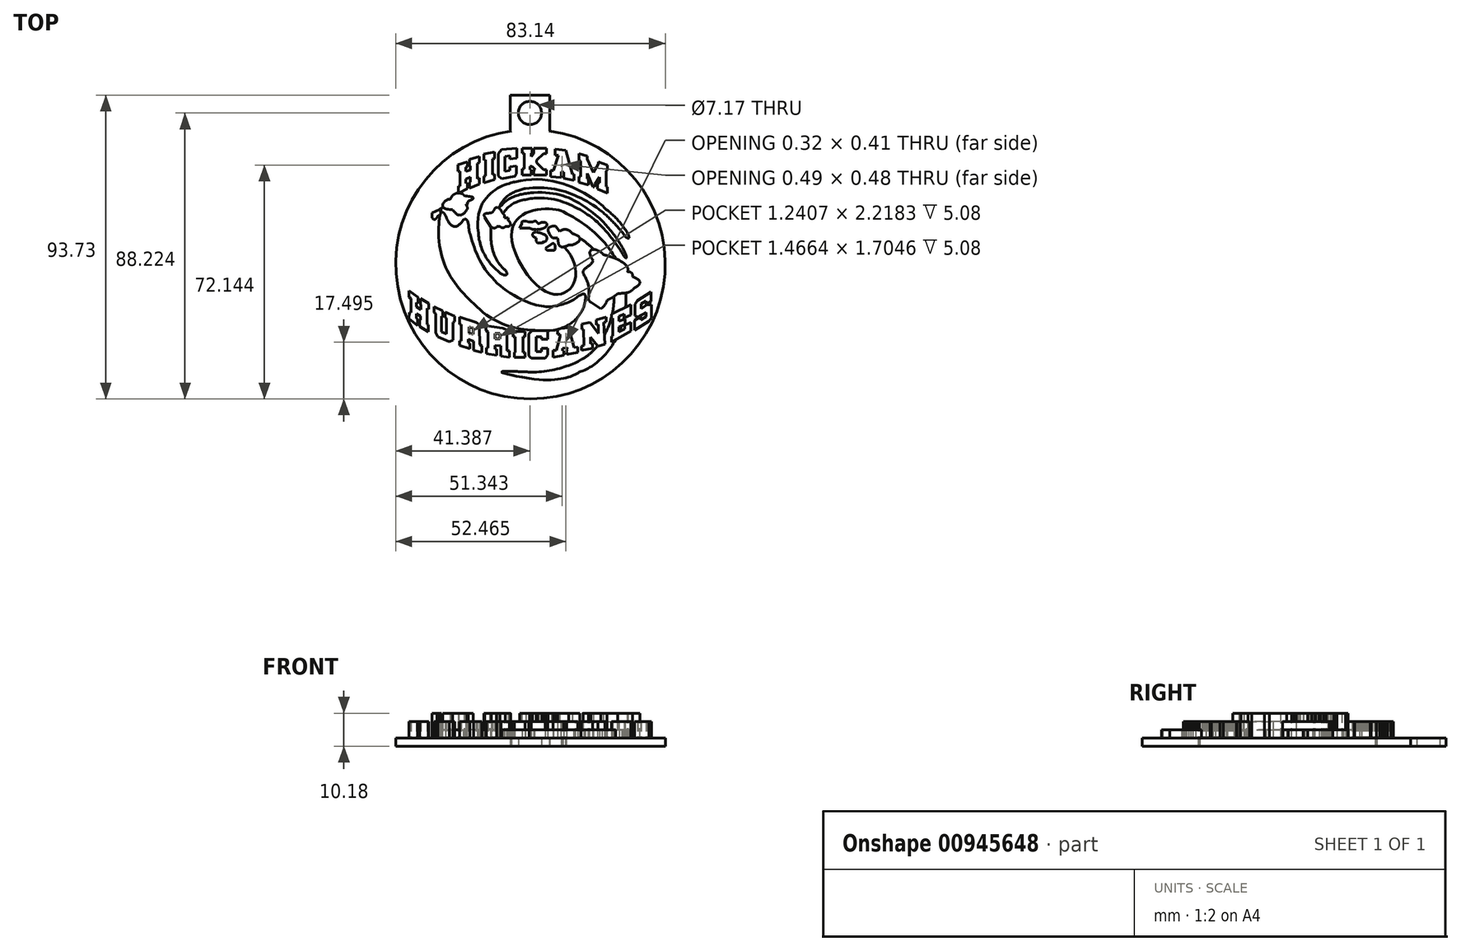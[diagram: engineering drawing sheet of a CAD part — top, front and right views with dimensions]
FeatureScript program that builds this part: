
annotation { "Feature Type Name" : "Feature", "Feature Type Description" : "" }
export const myFeature = defineFeature(function(context is Context, id is Id, definition is map)
    precondition{}
    {
        {
            var Q0;
            Q0=qCreatedBy(makeId("Top.planeOp"),FACE);
            var sketch = newSketch(context, id + "F0", { "sketchPlane" : qUnion([Q0])});
            skLineSegment(sketch, "E0", {"start": v(-15.9, 11.02) * mm, "end": v(-15.9, 12.89) * mm});
            skLineSegment(sketch, "E1", {"start": v(-15.9, 12.89) * mm, "end": v(-16.36, 12.66) * mm});
            skLineSegment(sketch, "E2", {"start": v(-16.36, 12.66) * mm, "end": v(-16.36, 13.98) * mm});
            skLineSegment(sketch, "E3", {"start": v(-16.36, 13.98) * mm, "end": v(-14.95, 14.61) * mm});
            skLineSegment(sketch, "E4", {"start": v(-14.95, 14.61) * mm, "end": v(-14.95, 13.09) * mm});
            skLineSegment(sketch, "E5", {"start": v(-14.95, 13.09) * mm, "end": v(-15.3, 12.92) * mm});
            skLineSegment(sketch, "E6", {"start": v(-15.3, 12.92) * mm, "end": v(-15.3, 11.2) * mm});
            skLineSegment(sketch, "E7", {"start": v(-15.3, 11.2) * mm, "end": v(-12.2, 12.5) * mm});
            skLineSegment(sketch, "E8", {"start": v(-12.2, 12.5) * mm, "end": v(-12.2, 14.33) * mm});
            skLineSegment(sketch, "E9", {"start": v(-12.2, 14.33) * mm, "end": v(-12.86, 14.15) * mm});
            skLineSegment(sketch, "E10", {"start": v(-12.86, 14.15) * mm, "end": v(-12.86, 18.85) * mm});
            skLineSegment(sketch, "E11", {"start": v(-12.2, 21) * mm, "end": v(-15.3, 20.05) * mm});
            skLineSegment(sketch, "E12", {"start": v(-15.3, 20.05) * mm, "end": v(-15.3, 18.1) * mm});
            skLineSegment(sketch, "E13", {"start": v(-15.3, 18.1) * mm, "end": v(-14.95, 18.1) * mm});
            skLineSegment(sketch, "E14", {"start": v(-14.95, 18.1) * mm, "end": v(-14.95, 16.73) * mm});
            skLineSegment(sketch, "E15", {"start": v(-14.95, 16.73) * mm, "end": v(-16.36, 16.33) * mm});
            skLineSegment(sketch, "E16", {"start": v(-16.36, 16.33) * mm, "end": v(-16.36, 17.7) * mm});
            skLineSegment(sketch, "E17", {"start": v(-16.36, 17.7) * mm, "end": v(-15.92, 17.83) * mm});
            skLineSegment(sketch, "E18", {"start": v(-15.92, 17.83) * mm, "end": v(-15.92, 19.28) * mm});
            skLineSegment(sketch, "E19", {"start": v(-15.92, 19.28) * mm, "end": v(-18.75, 18.48) * mm});
            skLineSegment(sketch, "E20", {"start": v(-18.75, 18.48) * mm, "end": v(-18.75, 16.33) * mm});
            skLineSegment(sketch, "E21", {"start": v(-18.75, 16.33) * mm, "end": v(-18.2, 16.33) * mm});
            skLineSegment(sketch, "E22", {"start": v(-18.2, 16.33) * mm, "end": v(-18.2, 11.8) * mm});
            skLineSegment(sketch, "E23", {"start": v(-15.9, 11.02) * mm, "end": v(-18.67, 9.58) * mm});
            skLineSegment(sketch, "E24", {"start": v(-18.67, 9.58) * mm, "end": v(-18.67, 11.8) * mm});
            skLineSegment(sketch, "E25", {"start": v(-18.67, 11.8) * mm, "end": v(-18.2, 11.8) * mm});
            skLineSegment(sketch, "E26", {"start": v(-12.2, 21) * mm, "end": v(-12.2, 19.06) * mm});
            skLineSegment(sketch, "E27", {"start": v(-12.86, 18.85) * mm, "end": v(-12.2, 19.06) * mm});
            skLineSegment(sketch, "E28", {"start": v(-7.48, 13.82) * mm, "end": v(-7.48, 15.47) * mm});
            skLineSegment(sketch, "E29", {"start": v(-8.17, 15.31) * mm, "end": v(-8.17, 20.25) * mm});
            skLineSegment(sketch, "E30", {"start": v(-10.78, 21.68) * mm, "end": v(-10.78, 19.77) * mm});
            skLineSegment(sketch, "E31", {"start": v(-10.78, 19.77) * mm, "end": v(-10.3, 19.9) * mm});
            skLineSegment(sketch, "E32", {"start": v(-10.3, 19.9) * mm, "end": v(-10.27, 14.93) * mm});
            skLineSegment(sketch, "E33", {"start": v(-10.78, 21.68) * mm, "end": v(-7.48, 22.33) * mm});
            skLineSegment(sketch, "E34", {"start": v(-8.17, 20.25) * mm, "end": v(-7.48, 20.36) * mm});
            skLineSegment(sketch, "E35", {"start": v(-7.48, 20.36) * mm, "end": v(-7.48, 22.33) * mm});
            skLineSegment(sketch, "E36", {"start": v(-8.17, 15.31) * mm, "end": v(-7.48, 15.47) * mm});
            skLineSegment(sketch, "E37", {"start": v(-10.27, 14.93) * mm, "end": v(-10.86, 14.8) * mm});
            skLineSegment(sketch, "E38", {"start": v(-7.48, 13.82) * mm, "end": v(-10.86, 12.88) * mm});
            skLineSegment(sketch, "E39", {"start": v(-10.86, 14.8) * mm, "end": v(-10.86, 12.88) * mm});
            skLineSegment(sketch, "E40", {"start": v(-0.78, 18.05) * mm, "end": v(-2.76, 17.8) * mm});
            skLineSegment(sketch, "E41", {"start": v(-0.78, 18.05) * mm, "end": v(-0.78, 15.68) * mm});
            skLineSegment(sketch, "E42", {"start": v(-0.78, 15.68) * mm, "end": v(-1.34, 14.9) * mm});
            skLineSegment(sketch, "E43", {"start": v(-1.34, 14.9) * mm, "end": v(-5.37, 14.1) * mm});
            skLineSegment(sketch, "E44", {"start": v(-5.37, 14.1) * mm, "end": v(-6.3, 14.95) * mm});
            skLineSegment(sketch, "E45", {"start": v(-6.3, 14.95) * mm, "end": v(-6.3, 21.84) * mm});
            skLineSegment(sketch, "E46", {"start": v(-6.3, 21.84) * mm, "end": v(-5.37, 23.14) * mm});
            skLineSegment(sketch, "E47", {"start": v(-2.76, 20.2) * mm, "end": v(-2.76, 21.22) * mm});
            skLineSegment(sketch, "E48", {"start": v(-2.76, 21.22) * mm, "end": v(-4.38, 21.01) * mm});
            skLineSegment(sketch, "E49", {"start": v(-4.38, 21.01) * mm, "end": v(-4.38, 16.43) * mm});
            skLineSegment(sketch, "E50", {"start": v(-2.76, 17.8) * mm, "end": v(-2.76, 16.63) * mm});
            skLineSegment(sketch, "E51", {"start": v(-4.38, 16.43) * mm, "end": v(-2.76, 16.63) * mm});
            skLineSegment(sketch, "E52", {"start": v(-5.37, 23.14) * mm, "end": v(-0.67, 23.5) * mm});
            skLineSegment(sketch, "E53", {"start": v(-2.76, 20.2) * mm, "end": v(-0.67, 20.42) * mm});
            skLineSegment(sketch, "E54", {"start": v(-0.67, 20.42) * mm, "end": v(-0.67, 23.5) * mm});
            skLineSegment(sketch, "E55", {"start": v(0.95, 15.2) * mm, "end": v(3.85, 15.2) * mm});
            skLineSegment(sketch, "E56", {"start": v(3.85, 15.2) * mm, "end": v(3.85, 16.84) * mm});
            skLineSegment(sketch, "E57", {"start": v(3.85, 16.84) * mm, "end": v(3.38, 16.84) * mm});
            skLineSegment(sketch, "E58", {"start": v(3.38, 16.84) * mm, "end": v(3.38, 17.88) * mm});
            skLineSegment(sketch, "E59", {"start": v(3.38, 17.88) * mm, "end": v(4.1, 17.88) * mm});
            skLineSegment(sketch, "E60", {"start": v(4.1, 17.88) * mm, "end": v(5.09, 16.84) * mm});
            skLineSegment(sketch, "E61", {"start": v(5.09, 16.84) * mm, "end": v(4.58, 16.84) * mm});
            skLineSegment(sketch, "E62", {"start": v(4.58, 16.84) * mm, "end": v(4.58, 15.23) * mm});
            skLineSegment(sketch, "E63", {"start": v(4.58, 15.23) * mm, "end": v(8.44, 15.23) * mm});
            skLineSegment(sketch, "E64", {"start": v(8.44, 15.23) * mm, "end": v(8.44, 16.84) * mm});
            skLineSegment(sketch, "E65", {"start": v(8.44, 16.84) * mm, "end": v(7.62, 16.84) * mm});
            skLineSegment(sketch, "E66", {"start": v(7.62, 16.84) * mm, "end": v(5.5, 19.1) * mm});
            skLineSegment(sketch, "E67", {"start": v(5.5, 19.1) * mm, "end": v(5.5, 19.83) * mm});
            skLineSegment(sketch, "E68", {"start": v(5.5, 19.83) * mm, "end": v(7.59, 21.8) * mm});
            skLineSegment(sketch, "E69", {"start": v(7.59, 21.8) * mm, "end": v(8.44, 21.8) * mm});
            skLineSegment(sketch, "E70", {"start": v(8.44, 21.8) * mm, "end": v(8.44, 23.54) * mm});
            skLineSegment(sketch, "E71", {"start": v(8.44, 23.54) * mm, "end": v(4.62, 23.54) * mm});
            skLineSegment(sketch, "E72", {"start": v(4.62, 23.54) * mm, "end": v(4.62, 21.8) * mm});
            skLineSegment(sketch, "E73", {"start": v(4.62, 21.8) * mm, "end": v(3.74, 20.97) * mm});
            skLineSegment(sketch, "E74", {"start": v(3.74, 20.97) * mm, "end": v(3.74, 21.96) * mm});
            skLineSegment(sketch, "E75", {"start": v(3.74, 21.96) * mm, "end": v(4.02, 21.96) * mm});
            skLineSegment(sketch, "E76", {"start": v(4.02, 21.96) * mm, "end": v(4.02, 23.54) * mm});
            skLineSegment(sketch, "E77", {"start": v(4.02, 23.54) * mm, "end": v(0.95, 23.54) * mm});
            skLineSegment(sketch, "E78", {"start": v(0.95, 23.54) * mm, "end": v(0.95, 21.96) * mm});
            skLineSegment(sketch, "E79", {"start": v(0.95, 21.96) * mm, "end": v(1.67, 21.96) * mm});
            skLineSegment(sketch, "E80", {"start": v(1.67, 21.96) * mm, "end": v(1.67, 17.11) * mm});
            skLineSegment(sketch, "E81", {"start": v(1.67, 17.11) * mm, "end": v(0.95, 17.11) * mm});
            skLineSegment(sketch, "E82", {"start": v(0.95, 17.11) * mm, "end": v(0.95, 15.2) * mm});
            skLineSegment(sketch, "E83", {"start": v(12.13, 21.38) * mm, "end": v(11.17, 21.38) * mm});
            skLineSegment(sketch, "E84", {"start": v(11.17, 21.38) * mm, "end": v(11.17, 23.25) * mm});
            skLineSegment(sketch, "E85", {"start": v(11.17, 23.25) * mm, "end": v(14.46, 22.88) * mm});
            skLineSegment(sketch, "E86", {"start": v(14.46, 22.88) * mm, "end": v(16.45, 15.55) * mm});
            skLineSegment(sketch, "E87", {"start": v(13.07, 16.29) * mm, "end": v(13.07, 14.48) * mm});
            skLineSegment(sketch, "E88", {"start": v(13.07, 14.48) * mm, "end": v(9.76, 14.7) * mm});
            skLineSegment(sketch, "E89", {"start": v(9.76, 14.7) * mm, "end": v(9.76, 16.7) * mm});
            skLineSegment(sketch, "E90", {"start": v(9.76, 16.7) * mm, "end": v(10.66, 16.7) * mm});
            skLineSegment(sketch, "E91", {"start": v(10.66, 16.7) * mm, "end": v(12.13, 21.38) * mm});
            skLineSegment(sketch, "E92", {"start": v(13.1, 18.18) * mm, "end": v(13.39, 18.54) * mm});
            skLineSegment(sketch, "E93", {"start": v(13.39, 18.54) * mm, "end": v(13.59, 18.06) * mm});
            skLineSegment(sketch, "E94", {"start": v(13.59, 18.06) * mm, "end": v(13.1, 18.18) * mm});
            skLineSegment(sketch, "E95", {"start": v(13.07, 16.29) * mm, "end": v(13.82, 16.2) * mm});
            skLineSegment(sketch, "E96", {"start": v(13.82, 16.2) * mm, "end": v(13.82, 14.2) * mm});
            skLineSegment(sketch, "E97", {"start": v(16.45, 15.55) * mm, "end": v(16.94, 15.46) * mm});
            skLineSegment(sketch, "E98", {"start": v(16.94, 15.46) * mm, "end": v(16.94, 13.6) * mm});
            skLineSegment(sketch, "E99", {"start": v(13.82, 14.2) * mm, "end": v(16.94, 13.6) * mm});
            skLineSegment(sketch, "E100", {"start": v(21.48, 12.18) * mm, "end": v(18.5, 12.97) * mm});
            skLineSegment(sketch, "E101", {"start": v(18.5, 12.97) * mm, "end": v(18.5, 14.78) * mm});
            skLineSegment(sketch, "E102", {"start": v(18.5, 14.78) * mm, "end": v(18.98, 14.78) * mm});
            skLineSegment(sketch, "E103", {"start": v(18.98, 14.78) * mm, "end": v(18.98, 19.51) * mm});
            skLineSegment(sketch, "E104", {"start": v(18.98, 19.51) * mm, "end": v(18.5, 19.64) * mm});
            skLineSegment(sketch, "E105", {"start": v(18.5, 19.64) * mm, "end": v(18.5, 21.8) * mm});
            skLineSegment(sketch, "E106", {"start": v(18.5, 21.8) * mm, "end": v(21.08, 21.1) * mm});
            skLineSegment(sketch, "E107", {"start": v(21.08, 21.1) * mm, "end": v(21.08, 20.15) * mm});
            skLineSegment(sketch, "E108", {"start": v(21.08, 20.15) * mm, "end": v(22.97, 16.06) * mm});
            skLineSegment(sketch, "E109", {"start": v(22.97, 16.06) * mm, "end": v(24.54, 18.63) * mm});
            skLineSegment(sketch, "E110", {"start": v(24.54, 18.63) * mm, "end": v(24.54, 19.35) * mm});
            skLineSegment(sketch, "E111", {"start": v(24.54, 19.35) * mm, "end": v(27.24, 18.35) * mm});
            skLineSegment(sketch, "E112", {"start": v(27.24, 18.35) * mm, "end": v(27.24, 16.71) * mm});
            skLineSegment(sketch, "E113", {"start": v(27.24, 16.71) * mm, "end": v(26.93, 16.5) * mm});
            skLineSegment(sketch, "E114", {"start": v(26.93, 16.5) * mm, "end": v(26.93, 11.65) * mm});
            skLineSegment(sketch, "E115", {"start": v(26.93, 11.65) * mm, "end": v(27.24, 11.57) * mm});
            skLineSegment(sketch, "E116", {"start": v(27.24, 11.57) * mm, "end": v(27.24, 9.63) * mm});
            skLineSegment(sketch, "E117", {"start": v(27.24, 9.63) * mm, "end": v(24.19, 10.96) * mm});
            skLineSegment(sketch, "E118", {"start": v(24.19, 10.96) * mm, "end": v(24.19, 12.77) * mm});
            skLineSegment(sketch, "E119", {"start": v(24.19, 12.77) * mm, "end": v(24.9, 12.77) * mm});
            skLineSegment(sketch, "E120", {"start": v(24.9, 12.77) * mm, "end": v(24.9, 14.55) * mm});
            skLineSegment(sketch, "E121", {"start": v(24.9, 14.55) * mm, "end": v(23.52, 12.5) * mm});
            skLineSegment(sketch, "E122", {"start": v(21.48, 12.18) * mm, "end": v(21.48, 13.92) * mm});
            skLineSegment(sketch, "E123", {"start": v(21.48, 13.92) * mm, "end": v(21.04, 14.1) * mm});
            skLineSegment(sketch, "E124", {"start": v(21.04, 14.1) * mm, "end": v(21.04, 15.72) * mm});
            skLineSegment(sketch, "E125", {"start": v(21.04, 15.72) * mm, "end": v(22.87, 11.57) * mm});
            skLineSegment(sketch, "E126", {"start": v(23.52, 12.5) * mm, "end": v(23.23, 11.57) * mm});
            skLineSegment(sketch, "E127", {"start": v(23.23, 11.57) * mm, "end": v(22.87, 11.57) * mm});
            skFitSpline(sketch, "E128", {"points": [v(13.96, -7.02) * mm, v(1.2, -13.5) * mm], "startDerivative": vector(28.65, -28.42) * mm, "endDerivative": vector(-33.16, 51.89) * mm});
            skFitSpline(sketch, "E129", {"points": [v(13.71, 3.88) * mm, v(19.16, -45.39) * mm], "startDerivative": vector(88.1, -43.97) * mm, "endDerivative": vector(-44.4, -16.38) * mm});
            skFitSpline(sketch, "E130", {"points": [v(19.35, -4.57) * mm, v(19.16, -41.7) * mm], "startDerivative": vector(52.93, -37.72) * mm, "endDerivative": vector(-25.1, -11.16) * mm});
            skFitSpline(sketch, "E131", {"points": [v(19.16, -41.7) * mm, v(3.28, -45.54) * mm], "startDerivative": vector(-8.69, -5.96) * mm, "endDerivative": vector(-15.97, 1.17) * mm});
            skFitSpline(sketch, "E132", {"points": [v(19.16, -45.39) * mm, v(3.2, -47.55) * mm], "startDerivative": vector(-1.7, 0.42) * mm, "endDerivative": vector(-36.36, 5.06) * mm});
            skFitSpline(sketch, "E133", {"points": [v(3.28, -45.54) * mm, v(3.2, -47.55) * mm], "startDerivative": vector(-5.26, -0.1) * mm, "endDerivative": vector(54.9, -9.72) * mm});
            skFitSpline(sketch, "E134", {"points": [v(15.42, -6.32) * mm, v(11.87, -4.23) * mm], "startDerivative": vector(-11.95, -6.26) * mm, "endDerivative": vector(-1.52, 1.7) * mm});
            skLineSegment(sketch, "E135", {"start": v(11.87, -4.23) * mm, "end": v(10.42, -4.23) * mm});
            skFitSpline(sketch, "E136", {"points": [v(10.42, -4.23) * mm, v(11.28, -0.5) * mm], "startDerivative": vector(-10.04, 11.34) * mm, "endDerivative": vector(2.08, 0) * mm});
            skLineSegment(sketch, "E137", {"start": v(11.28, -0.5) * mm, "end": v(12.5, -2.15) * mm});
            skFitSpline(sketch, "E138", {"points": [v(12.5, -2.15) * mm, v(16.55, -2.84) * mm], "startDerivative": vector(5.43, 4.15) * mm, "endDerivative": vector(2.26, -2.57) * mm});
            skLineSegment(sketch, "E139", {"start": v(10.71, -8.01) * mm, "end": v(9, -8.01) * mm});
            skLineSegment(sketch, "E140", {"start": v(8.34, -7.2) * mm, "end": v(9.99, -6.09) * mm});
            skLineSegment(sketch, "E141", {"start": v(11.22, -6.5) * mm, "end": v(11.22, -7.57) * mm});
            skFitSpline(sketch, "E142", {"points": [v(8.34, -7.2) * mm, v(9, -8.01) * mm], "startDerivative": vector(-0.6, -2.14) * mm, "endDerivative": vector(0.77, -0.2) * mm});
            skFitSpline(sketch, "E143", {"points": [v(9.99, -6.09) * mm, v(11.22, -6.5) * mm], "startDerivative": vector(1.76, 1.37) * mm, "endDerivative": vector(0.64, -1.41) * mm});
            skFitSpline(sketch, "E144", {"points": [v(11.22, -7.57) * mm, v(10.71, -8.01) * mm], "startDerivative": vector(-0.25, -0.9) * mm, "endDerivative": vector(-0.6, -0.04) * mm});
            skLineSegment(sketch, "E145", {"start": v(5.7, -5.73) * mm, "end": v(7.12, -5.73) * mm});
            skLineSegment(sketch, "E146", {"start": v(7.12, -5.73) * mm, "end": v(7.69, -5.32) * mm});
            skLineSegment(sketch, "E147", {"start": v(7.69, -5.32) * mm, "end": v(8.1, -5.28) * mm});
            skLineSegment(sketch, "E148", {"start": v(5.7, -5.73) * mm, "end": v(5.28, -5.17) * mm});
            skLineSegment(sketch, "E149", {"start": v(5.28, -5.17) * mm, "end": v(5.28, -4.15) * mm});
            skFitSpline(sketch, "E150", {"points": [v(5.28, -4.15) * mm, v(5.92, -2.5) * mm], "startDerivative": vector(-7.01, 2.92) * mm, "endDerivative": vector(2.93, -1.8) * mm});
            skFitSpline(sketch, "E151", {"points": [v(5.92, -2.5) * mm, v(8.1, -5.28) * mm], "startDerivative": vector(3.05, -0.1) * mm, "endDerivative": vector(-5.45, -4.94) * mm});
            skLineSegment(sketch, "E152", {"start": v(0.2, -1.11) * mm, "end": v(3.33, -1.11) * mm});
            skLineSegment(sketch, "E153", {"start": v(3.33, -1.11) * mm, "end": v(4.22, -1.54) * mm});
            skFitSpline(sketch, "E154", {"points": [v(4.22, -1.54) * mm, v(8.52, -0.45) * mm], "startDerivative": vector(9.88, -0.85) * mm, "endDerivative": vector(0.54, 0.89) * mm});
            skFitSpline(sketch, "E155", {"points": [v(6.16, 0.23) * mm, v(8.52, -0.45) * mm], "startDerivative": vector(2.01, 1.61) * mm, "endDerivative": vector(-1.5, -4.73) * mm});
            skFitSpline(sketch, "E156", {"points": [v(6.16, 0.23) * mm, v(4.29, 0.73) * mm], "startDerivative": vector(-2.47, 0.37) * mm, "endDerivative": vector(-3.96, -2.87) * mm});
            skLineSegment(sketch, "E157", {"start": v(4.29, 0.73) * mm, "end": v(3.03, 0.73) * mm});
            skLineSegment(sketch, "E158", {"start": v(3.03, 0.73) * mm, "end": v(2.19, 1.06) * mm});
            skLineSegment(sketch, "E159", {"start": v(0.2, -1.11) * mm, "end": v(0.9, 0.24) * mm});
            skFitSpline(sketch, "E160", {"points": [v(2.19, 1.06) * mm, v(0.9, 0.24) * mm], "startDerivative": vector(-1.28, -0.83) * mm, "endDerivative": vector(0.56, -3.5) * mm});
            skLineSegment(sketch, "E161", {"start": v(-10.5, 2.16) * mm, "end": v(-8.52, -0.97) * mm});
            skFitSpline(sketch, "E162", {"points": [v(-10.5, 2.16) * mm, v(-9.03, 3.6) * mm], "startDerivative": vector(-2.84, 5.24) * mm, "endDerivative": vector(1.46, 1.45) * mm});
            skFitSpline(sketch, "E163", {"points": [v(-9.03, 3.6) * mm, v(-7.2, 5.13) * mm], "startDerivative": vector(3.75, -0.63) * mm, "endDerivative": vector(1.83, 1.53) * mm});
            skFitSpline(sketch, "E164", {"points": [v(-7.2, 5.13) * mm, v(-4.47, 2.95) * mm], "startDerivative": vector(4.43, 2.28) * mm, "endDerivative": vector(2.96, -1.34) * mm});
            skLineSegment(sketch, "E165", {"start": v(-4.47, 2.95) * mm, "end": v(-4.47, 2.1) * mm});
            skFitSpline(sketch, "E166", {"points": [v(-3.26, 1.16) * mm, v(-4.16, -0.67) * mm], "startDerivative": vector(1.76, -1.34) * mm, "endDerivative": vector(-7.41, 0.54) * mm});
            skFitSpline(sketch, "E167", {"points": [v(-8.52, -0.97) * mm, v(-6.87, -0.68) * mm], "startDerivative": vector(2.38, -0.63) * mm, "endDerivative": vector(0.24, 1.44) * mm});
            skLineSegment(sketch, "E168", {"start": v(-6.87, -0.68) * mm, "end": v(-5.85, -0.68) * mm});
            skFitSpline(sketch, "E169", {"points": [v(-5.85, -0.68) * mm, v(-4.16, -0.67) * mm], "startDerivative": vector(2.5, -1.68) * mm, "endDerivative": vector(2.01, 1.38) * mm});
            skLineSegment(sketch, "E170", {"start": v(-4.47, 2.1) * mm, "end": v(-3.26, 2.1) * mm});
            skLineSegment(sketch, "E171", {"start": v(-3.26, 2.1) * mm, "end": v(-3.26, 1.16) * mm});
            skFitSpline(sketch, "E172", {"points": [v(-20.5, 4.52) * mm, v(-16, 4.62) * mm], "startDerivative": vector(5.62, -4.8) * mm, "endDerivative": vector(3.7, 4.3) * mm});
            skFitSpline(sketch, "E173", {"points": [v(-20.5, 4.52) * mm, v(-21.2, 7.76) * mm], "startDerivative": vector(-9, 2.88) * mm, "endDerivative": vector(4.02, 1.11) * mm});
            skFitSpline(sketch, "E174", {"points": [v(-21.2, 7.76) * mm, v(-16.87, 8.87) * mm], "startDerivative": vector(4.04, 4.92) * mm, "endDerivative": vector(2.25, -1.92) * mm});
            skFitSpline(sketch, "E175", {"points": [v(-16.87, 8.87) * mm, v(-15.62, 6.25) * mm], "startDerivative": vector(8.4, -2.4) * mm, "endDerivative": vector(0.82, -1.8) * mm});
            skFitSpline(sketch, "E176", {"points": [v(-15.62, 6.25) * mm, v(-16, 4.62) * mm], "startDerivative": vector(-1.92, -0.15) * mm, "endDerivative": vector(-0.39, -1.63) * mm});
            skLineSegment(sketch, "E177", {"start": v(-26.82, 3.55) * mm, "end": v(-26.82, 2.1) * mm});
            skFitSpline(sketch, "E178", {"points": [v(-26.82, 2.1) * mm, v(-25.34, 2.1) * mm], "startDerivative": vector(1.6, -2.72) * mm, "endDerivative": vector(0.97, 1.84) * mm});
            skFitSpline(sketch, "E179", {"points": [v(-25.34, 2.1) * mm, v(-24.13, 2.84) * mm], "startDerivative": vector(2.12, 3.3) * mm, "endDerivative": vector(0.74, 0.5) * mm});
            skLineSegment(sketch, "E180", {"start": v(-24.13, 2.84) * mm, "end": v(-24.13, 4.22) * mm});
            skFitSpline(sketch, "E181", {"points": [v(-24.13, 4.22) * mm, v(-24.58, 4.62) * mm], "startDerivative": vector(0.3, 1.46) * mm, "endDerivative": vector(-3.18, -2.54) * mm});
            skLineSegment(sketch, "E182", {"start": v(-24.58, 4.62) * mm, "end": v(-26.82, 3.55) * mm});
            skLineSegment(sketch, "E183", {"start": v(13.96, -7.02) * mm, "end": v(13.9, -6.91) * mm});
            skLineSegment(sketch, "E184", {"start": v(19.35, -4.57) * mm, "end": v(19.14, -4.43) * mm});
            skFitSpline(sketch, "E185", {"points": [v(22.93, -11.18) * mm, v(26.06, -9.3) * mm], "startDerivative": vector(-8.98, 13.05) * mm, "endDerivative": vector(5.74, -6.62) * mm});
            skFitSpline(sketch, "E186", {"points": [v(26.06, -9.3) * mm, v(33.58, -14.65) * mm], "startDerivative": vector(29.23, -7.93) * mm, "endDerivative": vector(1.02, 0) * mm});
            skFitSpline(sketch, "E187", {"points": [v(33.58, -14.65) * mm, v(35.09, -16.14) * mm], "startDerivative": vector(3.62, 0.47) * mm, "endDerivative": vector(-0.34, -2.03) * mm});
            skFitSpline(sketch, "E188", {"points": [v(35.09, -16.14) * mm, v(35.09, -20.1) * mm], "startDerivative": vector(14.76, -5.46) * mm, "endDerivative": vector(-0.77, -1.8) * mm});
            skFitSpline(sketch, "E189", {"points": [v(35.09, -20.1) * mm, v(30.5, -21.3) * mm], "startDerivative": vector(-3.29, -3.8) * mm, "endDerivative": vector(-3.27, -0.11) * mm});
            skFitSpline(sketch, "E190", {"points": [v(30.5, -21.3) * mm, v(27.21, -23.35) * mm], "startDerivative": vector(-2.66, -2.5) * mm, "endDerivative": vector(-3.77, -1.64) * mm});
            skFitSpline(sketch, "E191", {"points": [v(27.21, -23.35) * mm, v(25.28, -25.97) * mm], "startDerivative": vector(-0.86, -3.56) * mm, "endDerivative": vector(-1.28, -0.16) * mm});
            skLineSegment(sketch, "E192", {"start": v(25.28, -25.97) * mm, "end": v(22.2, -24.06) * mm});
            skFitSpline(sketch, "E193", {"points": [v(22.2, -24.06) * mm, v(21.5, -22.52) * mm], "startDerivative": vector(-1.6, 1.12) * mm, "endDerivative": vector(0.32, 2.23) * mm});
            skFitSpline(sketch, "E194", {"points": [v(20.02, -15.5) * mm, v(21.5, -22.52) * mm], "startDerivative": vector(4.63, -7.34) * mm, "endDerivative": vector(-0.96, -8.3) * mm});
            skFitSpline(sketch, "E195", {"points": [v(22.93, -11.18) * mm, v(20.02, -15.5) * mm], "startDerivative": vector(-3.93, -7.23) * mm, "endDerivative": vector(3.5, -5.58) * mm});
            skFitSpline(sketch, "E196", {"points": [v(16.9, -23.22) * mm, v(20.03, -25.3) * mm], "startDerivative": vector(11.17, 8.61) * mm, "endDerivative": vector(-3.35, -13.4) * mm});
            skFitSpline(sketch, "E197", {"points": [v(16.9, -23.22) * mm, v(0.99, -23.22) * mm], "startDerivative": vector(-11.86, -5.92) * mm, "endDerivative": vector(-21.63, 10.86) * mm});
            skFitSpline(sketch, "E198", {"points": [v(0.99, -23.22) * mm, v(-15.03, -3) * mm], "startDerivative": vector(-30.7, 14.84) * mm, "endDerivative": vector(-6.1, 23.91) * mm});
            skFitSpline(sketch, "E199", {"points": [v(-22.56, 2.62) * mm, v(-17.21, 1.36) * mm], "startDerivative": vector(4.1, -12.33) * mm, "endDerivative": vector(4.96, 8.35) * mm});
            skFitSpline(sketch, "E200", {"points": [v(-17.21, 1.36) * mm, v(-15.03, -3) * mm], "startDerivative": vector(6.1, 4.29) * mm, "endDerivative": vector(2.18, -4.37) * mm});
            skFitSpline(sketch, "E201", {"points": [v(-22.56, 2.62) * mm, v(-24.73, -1.27) * mm], "startDerivative": vector(-6.06, 11.35) * mm, "endDerivative": vector(0, -3.81) * mm});
            skFitSpline(sketch, "E202", {"points": [v(-24.73, -1.27) * mm, v(-13.89, -24.49) * mm], "startDerivative": vector(-1.27, -31.56) * mm, "endDerivative": vector(19.05, -17.17) * mm});
            skFitSpline(sketch, "E203", {"points": [v(-13.89, -24.49) * mm, v(10.7, -32.7) * mm], "startDerivative": vector(21.43, -23) * mm, "endDerivative": vector(27.1, 1.07) * mm});
            skFitSpline(sketch, "E204", {"points": [v(20.03, -25.3) * mm, v(10.7, -32.7) * mm], "startDerivative": vector(-4.14, -12.54) * mm, "endDerivative": vector(-12.34, -2.41) * mm});
            skFitSpline(sketch, "E205", {"points": [v(-6.18, -14.6) * mm, v(-4.85, -13.53) * mm], "startDerivative": vector(5.5, -5.94) * mm, "endDerivative": vector(-7.6, 6.06) * mm});
            skFitSpline(sketch, "E206", {"points": [v(-6.18, -14.6) * mm, v(-12.52, -2.72) * mm], "startDerivative": vector(-9.85, 7.54) * mm, "endDerivative": vector(-1.06, 15.01) * mm});
            skFitSpline(sketch, "E207", {"points": [v(-8.52, -0.97) * mm, v(-4.85, -13.53) * mm], "startDerivative": vector(-1.74, -14.33) * mm, "endDerivative": vector(9.08, -8.33) * mm});
            skFitSpline(sketch, "E208", {"points": [v(-12.52, -2.72) * mm, v(-1.28, 13.14) * mm], "startDerivative": vector(-5.31, 39.28) * mm, "endDerivative": vector(6.71, 1.85) * mm});
            skFitSpline(sketch, "E209", {"points": [v(-1.28, 13.14) * mm, v(26.54, 4.92) * mm], "startDerivative": vector(40.4, 10.66) * mm, "endDerivative": vector(5.1, -6.95) * mm});
            skFitSpline(sketch, "E210", {"points": [v(-6.08, 5.03) * mm, v(4.5, 9.82) * mm], "startDerivative": vector(8.8, 12.14) * mm, "endDerivative": vector(9.41, 0.8) * mm});
            skFitSpline(sketch, "E211", {"points": [v(4.5, 9.82) * mm, v(24.93, 1.85) * mm], "startDerivative": vector(30.79, 1.6) * mm, "endDerivative": vector(15.8, -12.76) * mm});
            skFitSpline(sketch, "E212", {"points": [v(-4.97, 3.4) * mm, v(4.77, 8.12) * mm], "startDerivative": vector(7.69, 10.68) * mm, "endDerivative": vector(14.32, 2.07) * mm});
            skFitSpline(sketch, "E213", {"points": [v(4.77, 8.12) * mm, v(24.23, 0.73) * mm], "startDerivative": vector(24.4, 2.07) * mm, "endDerivative": vector(12.6, -10.53) * mm});
            skFitSpline(sketch, "E214", {"points": [v(-6.08, 5.03) * mm, v(2.01, 11.1) * mm], "startDerivative": vector(4.03, 12.97) * mm, "endDerivative": vector(8.18, 2.15) * mm});
            skFitSpline(sketch, "E215", {"points": [v(2.01, 11.1) * mm, v(25.64, 3.96) * mm], "startDerivative": vector(27.42, 3.55) * mm, "endDerivative": vector(20.66, -15.83) * mm});
            skFitSpline(sketch, "E216", {"points": [v(24.23, 0.73) * mm, v(32.09, -9.3) * mm], "startDerivative": vector(9.37, -9.7) * mm, "endDerivative": vector(5.42, -9.9) * mm});
            skFitSpline(sketch, "E217", {"points": [v(24.93, 1.85) * mm, v(32.78, -8.72) * mm], "startDerivative": vector(9.53, -9.38) * mm, "endDerivative": vector(5.58, -11) * mm});
            skFitSpline(sketch, "E218", {"points": [v(32.09, -9.3) * mm, v(32.78, -8.72) * mm], "startDerivative": vector(3.8, -5.53) * mm, "endDerivative": vector(-1.87, 5.07) * mm});
            skFitSpline(sketch, "E219", {"points": [v(25.64, 3.96) * mm, v(32.81, -3.67) * mm], "startDerivative": vector(7.96, -6.95) * mm, "endDerivative": vector(6.7, -8.93) * mm});
            skFitSpline(sketch, "E220", {"points": [v(26.54, 4.92) * mm, v(33.56, -2.77) * mm], "startDerivative": vector(9.73, -6.94) * mm, "endDerivative": vector(5.1, -8.3) * mm});
            skFitSpline(sketch, "E221", {"points": [v(33.56, -2.77) * mm, v(32.81, -3.67) * mm], "startDerivative": vector(2.63, -5.02) * mm, "endDerivative": vector(-2.87, 3.03) * mm});
            skLineSegment(sketch, "E222", {"start": v(-33.93, -29.07) * mm, "end": v(-31.27, -31.25) * mm});
            skLineSegment(sketch, "E223", {"start": v(-31.27, -31.25) * mm, "end": v(-31.27, -29.23) * mm});
            skLineSegment(sketch, "E224", {"start": v(-31.67, -28.92) * mm, "end": v(-31.67, -27.53) * mm});
            skLineSegment(sketch, "E225", {"start": v(-31.67, -27.53) * mm, "end": v(-30.37, -28.34) * mm});
            skLineSegment(sketch, "E226", {"start": v(-30.37, -28.34) * mm, "end": v(-30.37, -29.48) * mm});
            skLineSegment(sketch, "E227", {"start": v(-30.37, -29.48) * mm, "end": v(-30.62, -29.48) * mm});
            skLineSegment(sketch, "E228", {"start": v(-30.62, -29.48) * mm, "end": v(-30.62, -31.49) * mm});
            skLineSegment(sketch, "E229", {"start": v(-30.62, -31.49) * mm, "end": v(-27.93, -33.14) * mm});
            skLineSegment(sketch, "E230", {"start": v(-27.93, -33.14) * mm, "end": v(-27.93, -31.04) * mm});
            skLineSegment(sketch, "E231", {"start": v(-27.93, -31.04) * mm, "end": v(-28.27, -30.84) * mm});
            skLineSegment(sketch, "E232", {"start": v(-28.27, -30.84) * mm, "end": v(-28.27, -25.96) * mm});
            skLineSegment(sketch, "E233", {"start": v(-28.27, -25.96) * mm, "end": v(-27.87, -26.19) * mm});
            skLineSegment(sketch, "E234", {"start": v(-31.27, -29.23) * mm, "end": v(-31.67, -28.92) * mm});
            skLineSegment(sketch, "E235", {"start": v(-27.87, -26.19) * mm, "end": v(-27.87, -24.4) * mm});
            skLineSegment(sketch, "E236", {"start": v(-27.87, -24.4) * mm, "end": v(-30.37, -22.81) * mm});
            skLineSegment(sketch, "E237", {"start": v(-30.37, -22.81) * mm, "end": v(-30.37, -24.71) * mm});
            skLineSegment(sketch, "E238", {"start": v(-30.37, -24.71) * mm, "end": v(-30.17, -24.82) * mm});
            skLineSegment(sketch, "E239", {"start": v(-30.17, -24.82) * mm, "end": v(-30.17, -26.26) * mm});
            skLineSegment(sketch, "E240", {"start": v(-30.17, -26.26) * mm, "end": v(-31.62, -25.46) * mm});
            skLineSegment(sketch, "E241", {"start": v(-31.62, -25.46) * mm, "end": v(-31.62, -24.13) * mm});
            skLineSegment(sketch, "E242", {"start": v(-31.62, -24.13) * mm, "end": v(-31.14, -24.33) * mm});
            skLineSegment(sketch, "E243", {"start": v(-31.14, -24.33) * mm, "end": v(-31.14, -22.52) * mm});
            skLineSegment(sketch, "E244", {"start": v(-31.14, -22.52) * mm, "end": v(-33.9, -20.43) * mm});
            skLineSegment(sketch, "E245", {"start": v(-33.9, -20.43) * mm, "end": v(-33.9, -22.52) * mm});
            skLineSegment(sketch, "E246", {"start": v(-33.9, -22.52) * mm, "end": v(-33.31, -22.81) * mm});
            skLineSegment(sketch, "E247", {"start": v(-33.31, -22.81) * mm, "end": v(-33.31, -27.15) * mm});
            skLineSegment(sketch, "E248", {"start": v(-33.31, -27.15) * mm, "end": v(-33.85, -27.15) * mm});
            skLineSegment(sketch, "E249", {"start": v(-33.85, -27.15) * mm, "end": v(-33.93, -29.07) * mm});
            skLineSegment(sketch, "E250", {"start": v(-26.24, -27.15) * mm, "end": v(-25.73, -27.5) * mm});
            skLineSegment(sketch, "E251", {"start": v(-25.73, -27.5) * mm, "end": v(-25.73, -33.38) * mm});
            skLineSegment(sketch, "E252", {"start": v(-25.73, -33.38) * mm, "end": v(-25.01, -34.7) * mm});
            skLineSegment(sketch, "E253", {"start": v(-25.01, -34.7) * mm, "end": v(-21.53, -36.22) * mm});
            skLineSegment(sketch, "E254", {"start": v(-21.53, -36.22) * mm, "end": v(-20.36, -35.73) * mm});
            skLineSegment(sketch, "E255", {"start": v(-20.36, -35.73) * mm, "end": v(-20.36, -30.19) * mm});
            skLineSegment(sketch, "E256", {"start": v(-20.36, -30.19) * mm, "end": v(-19.8, -29.99) * mm});
            skLineSegment(sketch, "E257", {"start": v(-19.8, -29.99) * mm, "end": v(-19.8, -28.33) * mm});
            skLineSegment(sketch, "E258", {"start": v(-19.8, -28.33) * mm, "end": v(-22.78, -27.08) * mm});
            skLineSegment(sketch, "E259", {"start": v(-22.78, -27.08) * mm, "end": v(-22.78, -28.71) * mm});
            skLineSegment(sketch, "E260", {"start": v(-22.78, -28.71) * mm, "end": v(-22.42, -28.91) * mm});
            skLineSegment(sketch, "E261", {"start": v(-22.42, -28.91) * mm, "end": v(-22.42, -33.79) * mm});
            skLineSegment(sketch, "E262", {"start": v(-22.42, -33.79) * mm, "end": v(-23.94, -33.12) * mm});
            skLineSegment(sketch, "E263", {"start": v(-23.94, -33.12) * mm, "end": v(-23.94, -28.38) * mm});
            skLineSegment(sketch, "E264", {"start": v(-23.94, -28.38) * mm, "end": v(-23.5, -28.65) * mm});
            skLineSegment(sketch, "E265", {"start": v(-23.5, -28.65) * mm, "end": v(-23.5, -26.68) * mm});
            skLineSegment(sketch, "E266", {"start": v(-23.5, -26.68) * mm, "end": v(-26.24, -25.38) * mm});
            skLineSegment(sketch, "E267", {"start": v(-26.24, -25.38) * mm, "end": v(-26.24, -27.15) * mm});
            skLineSegment(sketch, "E268", {"start": v(-17.78, -30.87) * mm, "end": v(-18.31, -30.87) * mm});
            skLineSegment(sketch, "E269", {"start": v(-18.31, -30.87) * mm, "end": v(-18.31, -28.58) * mm});
            skLineSegment(sketch, "E270", {"start": v(-18.31, -28.58) * mm, "end": v(-13.2, -30.23) * mm});
            skFitSpline(sketch, "E271", {"points": [v(-13.2, -30.23) * mm, v(-12.14, -31.88) * mm], "startDerivative": vector(2.26, -1.27) * mm, "endDerivative": vector(-0.5, -2.47) * mm});
            skLineSegment(sketch, "E272", {"start": v(-17.78, -30.87) * mm, "end": v(-17.78, -35.9) * mm});
            skLineSegment(sketch, "E273", {"start": v(-17.78, -35.9) * mm, "end": v(-18.33, -35.9) * mm});
            skLineSegment(sketch, "E274", {"start": v(-18.33, -35.9) * mm, "end": v(-18.33, -37.36) * mm});
            skLineSegment(sketch, "E275", {"start": v(-18.33, -37.36) * mm, "end": v(-15.1, -38.32) * mm});
            skLineSegment(sketch, "E276", {"start": v(-15.1, -38.32) * mm, "end": v(-15.1, -36.68) * mm});
            skLineSegment(sketch, "E277", {"start": v(-15.1, -36.68) * mm, "end": v(-15.59, -36.48) * mm});
            skLineSegment(sketch, "E278", {"start": v(-15.59, -36.48) * mm, "end": v(-15.59, -35.43) * mm});
            skLineSegment(sketch, "E279", {"start": v(-15.59, -35.43) * mm, "end": v(-13.96, -36.08) * mm});
            skLineSegment(sketch, "E280", {"start": v(-13.96, -36.08) * mm, "end": v(-13.96, -38.81) * mm});
            skLineSegment(sketch, "E281", {"start": v(-13.96, -38.81) * mm, "end": v(-11.42, -39.44) * mm});
            skLineSegment(sketch, "E282", {"start": v(-11.42, -39.44) * mm, "end": v(-11.42, -37.51) * mm});
            skLineSegment(sketch, "E283", {"start": v(-11.42, -37.51) * mm, "end": v(-12.13, -37.1) * mm});
            skLineSegment(sketch, "E284", {"start": v(-12.13, -37.1) * mm, "end": v(-12.14, -31.88) * mm});
            skLineSegment(sketch, "E285", {"start": v(-15.37, -31.66) * mm, "end": v(-14.13, -32) * mm});
            skLineSegment(sketch, "E286", {"start": v(-14.13, -32) * mm, "end": v(-14.13, -33.88) * mm});
            skLineSegment(sketch, "E287", {"start": v(-14.13, -33.88) * mm, "end": v(-15.37, -33.5) * mm});
            skLineSegment(sketch, "E288", {"start": v(-15.37, -33.5) * mm, "end": v(-15.37, -31.66) * mm});
            skLineSegment(sketch, "E289", {"start": v(-10.02, -38.1) * mm, "end": v(-9.54, -38.1) * mm});
            skLineSegment(sketch, "E290", {"start": v(-9.54, -38.1) * mm, "end": v(-9.54, -33.2) * mm});
            skLineSegment(sketch, "E291", {"start": v(-9.54, -33.2) * mm, "end": v(-10.18, -32.78) * mm});
            skLineSegment(sketch, "E292", {"start": v(-10.18, -32.78) * mm, "end": v(-10.18, -31.24) * mm});
            skLineSegment(sketch, "E293", {"start": v(-10.18, -31.24) * mm, "end": v(-5.05, -32.01) * mm});
            skFitSpline(sketch, "E294", {"points": [v(-5.05, -32.01) * mm, v(-3.7, -33.66) * mm], "startDerivative": vector(2.09, -0.85) * mm, "endDerivative": vector(-0.19, -4.36) * mm});
            skLineSegment(sketch, "E295", {"start": v(-3.7, -33.66) * mm, "end": v(-3.7, -39) * mm});
            skLineSegment(sketch, "E296", {"start": v(-3.7, -39) * mm, "end": v(-3, -39) * mm});
            skLineSegment(sketch, "E297", {"start": v(-3, -39) * mm, "end": v(-3, -40.96) * mm});
            skLineSegment(sketch, "E298", {"start": v(-3, -40.96) * mm, "end": v(-5.65, -40.65) * mm});
            skLineSegment(sketch, "E299", {"start": v(-5.65, -40.65) * mm, "end": v(-5.65, -37.48) * mm});
            skLineSegment(sketch, "E300", {"start": v(-5.65, -37.48) * mm, "end": v(-7.4, -37.33) * mm});
            skLineSegment(sketch, "E301", {"start": v(-7.4, -37.33) * mm, "end": v(-7.4, -38.47) * mm});
            skLineSegment(sketch, "E302", {"start": v(-7.4, -38.47) * mm, "end": v(-6.83, -38.47) * mm});
            skLineSegment(sketch, "E303", {"start": v(-6.83, -38.47) * mm, "end": v(-6.83, -40.44) * mm});
            skLineSegment(sketch, "E304", {"start": v(-6.83, -40.44) * mm, "end": v(-10.02, -39.87) * mm});
            skLineSegment(sketch, "E305", {"start": v(-10.02, -39.87) * mm, "end": v(-10.02, -38.1) * mm});
            skLineSegment(sketch, "E306", {"start": v(-7.34, -35.36) * mm, "end": v(-5.88, -35.36) * mm});
            skLineSegment(sketch, "E307", {"start": v(-5.88, -35.36) * mm, "end": v(-5.88, -33.66) * mm});
            skLineSegment(sketch, "E308", {"start": v(-5.88, -33.66) * mm, "end": v(-7.34, -33.66) * mm});
            skLineSegment(sketch, "E309", {"start": v(-1.44, -40.98) * mm, "end": v(1.85, -40.98) * mm});
            skLineSegment(sketch, "E310", {"start": v(1.85, -40.98) * mm, "end": v(1.85, -39.52) * mm});
            skLineSegment(sketch, "E311", {"start": v(1.85, -39.52) * mm, "end": v(1.22, -39.52) * mm});
            skLineSegment(sketch, "E312", {"start": v(1.22, -39.52) * mm, "end": v(1.22, -34.72) * mm});
            skLineSegment(sketch, "E313", {"start": v(1.22, -34.72) * mm, "end": v(1.85, -34.72) * mm});
            skLineSegment(sketch, "E314", {"start": v(1.85, -34.72) * mm, "end": v(1.85, -33.05) * mm});
            skLineSegment(sketch, "E315", {"start": v(1.85, -33.05) * mm, "end": v(-1.72, -33.05) * mm});
            skLineSegment(sketch, "E316", {"start": v(-1.72, -33.05) * mm, "end": v(-1.72, -34.72) * mm});
            skLineSegment(sketch, "E317", {"start": v(-1.72, -34.72) * mm, "end": v(-1.11, -34.72) * mm});
            skLineSegment(sketch, "E318", {"start": v(-1.11, -34.72) * mm, "end": v(-1.11, -39.52) * mm});
            skLineSegment(sketch, "E319", {"start": v(-1.11, -39.52) * mm, "end": v(-1.44, -39.52) * mm});
            skLineSegment(sketch, "E320", {"start": v(-1.44, -39.52) * mm, "end": v(-1.44, -40.98) * mm});
            skLineSegment(sketch, "E321", {"start": v(7.03, -38.25) * mm, "end": v(8.86, -38.25) * mm});
            skLineSegment(sketch, "E322", {"start": v(8.86, -38.25) * mm, "end": v(8.86, -40.27) * mm});
            skLineSegment(sketch, "E323", {"start": v(8.86, -40.27) * mm, "end": v(8.06, -41.23) * mm});
            skLineSegment(sketch, "E324", {"start": v(8.06, -41.23) * mm, "end": v(3.84, -41.23) * mm});
            skLineSegment(sketch, "E325", {"start": v(3.84, -41.23) * mm, "end": v(3.07, -40.54) * mm});
            skLineSegment(sketch, "E326", {"start": v(3.07, -40.54) * mm, "end": v(3.07, -33.8) * mm});
            skLineSegment(sketch, "E327", {"start": v(3.07, -33.8) * mm, "end": v(4.01, -32.78) * mm});
            skLineSegment(sketch, "E328", {"start": v(4.01, -32.78) * mm, "end": v(8.88, -32.78) * mm});
            skLineSegment(sketch, "E329", {"start": v(8.88, -32.78) * mm, "end": v(8.88, -35.38) * mm});
            skLineSegment(sketch, "E330", {"start": v(8.88, -35.38) * mm, "end": v(7.03, -35.38) * mm});
            skLineSegment(sketch, "E331", {"start": v(7.03, -35.38) * mm, "end": v(7.03, -34.72) * mm});
            skLineSegment(sketch, "E332", {"start": v(7.03, -34.72) * mm, "end": v(5.35, -34.72) * mm});
            skLineSegment(sketch, "E333", {"start": v(5.35, -34.72) * mm, "end": v(5.35, -39.26) * mm});
            skLineSegment(sketch, "E334", {"start": v(5.35, -39.26) * mm, "end": v(7.03, -39.26) * mm});
            skLineSegment(sketch, "E335", {"start": v(7.03, -39.26) * mm, "end": v(7.03, -38.25) * mm});
            skLineSegment(sketch, "E336", {"start": v(10.47, -38.88) * mm, "end": v(10.47, -40.98) * mm});
            skLineSegment(sketch, "E337", {"start": v(10.47, -40.98) * mm, "end": v(13.87, -40.37) * mm});
            skLineSegment(sketch, "E338", {"start": v(13.87, -40.37) * mm, "end": v(13.87, -39.01) * mm});
            skLineSegment(sketch, "E339", {"start": v(13.87, -39.01) * mm, "end": v(13.5, -39.01) * mm});
            skLineSegment(sketch, "E340", {"start": v(13.5, -39.01) * mm, "end": v(13.5, -38.25) * mm});
            skLineSegment(sketch, "E341", {"start": v(13.5, -38.25) * mm, "end": v(14.9, -38.1) * mm});
            skLineSegment(sketch, "E342", {"start": v(14.9, -38.1) * mm, "end": v(15.14, -38.48) * mm});
            skLineSegment(sketch, "E343", {"start": v(15.14, -38.48) * mm, "end": v(14.69, -38.58) * mm});
            skLineSegment(sketch, "E344", {"start": v(14.69, -38.58) * mm, "end": v(14.69, -40.14) * mm});
            skLineSegment(sketch, "E345", {"start": v(14.69, -40.14) * mm, "end": v(18.09, -39.52) * mm});
            skLineSegment(sketch, "E346", {"start": v(18.09, -37.8) * mm, "end": v(18.09, -39.52) * mm});
            skLineSegment(sketch, "E347", {"start": v(18.09, -37.8) * mm, "end": v(17.06, -37.93) * mm});
            skLineSegment(sketch, "E348", {"start": v(17.06, -37.93) * mm, "end": v(15.35, -31.89) * mm});
            skLineSegment(sketch, "E349", {"start": v(15.35, -31.89) * mm, "end": v(11.98, -32.15) * mm});
            skLineSegment(sketch, "E350", {"start": v(11.98, -32.15) * mm, "end": v(11.98, -33.87) * mm});
            skLineSegment(sketch, "E351", {"start": v(11.98, -33.87) * mm, "end": v(12.64, -33.87) * mm});
            skLineSegment(sketch, "E352", {"start": v(12.64, -33.87) * mm, "end": v(12.64, -34.72) * mm});
            skLineSegment(sketch, "E353", {"start": v(12.64, -34.72) * mm, "end": v(11.51, -38.81) * mm});
            skLineSegment(sketch, "E354", {"start": v(11.51, -38.81) * mm, "end": v(10.47, -38.88) * mm});
            skLineSegment(sketch, "E355", {"start": v(14.3, -36.55) * mm, "end": v(14.62, -36.55) * mm});
            skLineSegment(sketch, "E356", {"start": v(14.62, -36.55) * mm, "end": v(14.45, -36.14) * mm});
            skLineSegment(sketch, "E357", {"start": v(14.45, -36.14) * mm, "end": v(14.3, -36.55) * mm});
            skLineSegment(sketch, "E358", {"start": v(20.07, -37.37) * mm, "end": v(19.32, -37.58) * mm});
            skLineSegment(sketch, "E359", {"start": v(19.32, -37.58) * mm, "end": v(19.32, -38.88) * mm});
            skLineSegment(sketch, "E360", {"start": v(19.32, -38.88) * mm, "end": v(22.69, -38.25) * mm});
            skLineSegment(sketch, "E361", {"start": v(22.69, -38.25) * mm, "end": v(22.69, -36.7) * mm});
            skLineSegment(sketch, "E362", {"start": v(22.69, -36.7) * mm, "end": v(22.1, -36.85) * mm});
            skLineSegment(sketch, "E363", {"start": v(22.1, -36.85) * mm, "end": v(22.1, -34.84) * mm});
            skLineSegment(sketch, "E364", {"start": v(22.1, -34.84) * mm, "end": v(24.38, -37.53) * mm});
            skLineSegment(sketch, "E365", {"start": v(24.38, -37.53) * mm, "end": v(26.5, -36.97) * mm});
            skLineSegment(sketch, "E366", {"start": v(26.5, -36.97) * mm, "end": v(26.19, -30.23) * mm});
            skLineSegment(sketch, "E367", {"start": v(26.19, -30.23) * mm, "end": v(26.86, -30.05) * mm});
            skLineSegment(sketch, "E368", {"start": v(26.86, -30.05) * mm, "end": v(26.86, -28.58) * mm});
            skLineSegment(sketch, "E369", {"start": v(26.86, -28.58) * mm, "end": v(23.92, -29.48) * mm});
            skLineSegment(sketch, "E370", {"start": v(23.92, -29.48) * mm, "end": v(23.92, -31.02) * mm});
            skLineSegment(sketch, "E371", {"start": v(23.92, -31.02) * mm, "end": v(24.55, -30.81) * mm});
            skLineSegment(sketch, "E372", {"start": v(24.55, -30.81) * mm, "end": v(24.55, -33.64) * mm});
            skLineSegment(sketch, "E373", {"start": v(24.55, -33.64) * mm, "end": v(21.92, -30.23) * mm});
            skLineSegment(sketch, "E374", {"start": v(21.92, -30.23) * mm, "end": v(19.47, -30.69) * mm});
            skLineSegment(sketch, "E375", {"start": v(19.47, -30.69) * mm, "end": v(19.47, -32.38) * mm});
            skLineSegment(sketch, "E376", {"start": v(19.47, -32.38) * mm, "end": v(19.93, -32.38) * mm});
            skLineSegment(sketch, "E377", {"start": v(19.93, -32.38) * mm, "end": v(20.07, -37.37) * mm});
            skLineSegment(sketch, "E378", {"start": v(34.5, -32.94) * mm, "end": v(28.57, -36.27) * mm});
            skLineSegment(sketch, "E379", {"start": v(28.57, -36.27) * mm, "end": v(28.57, -34.56) * mm});
            skLineSegment(sketch, "E380", {"start": v(28.57, -34.56) * mm, "end": v(28.89, -34.4) * mm});
            skLineSegment(sketch, "E381", {"start": v(28.89, -34.4) * mm, "end": v(28.89, -29) * mm});
            skLineSegment(sketch, "E382", {"start": v(28.89, -29) * mm, "end": v(28.57, -29.15) * mm});
            skLineSegment(sketch, "E383", {"start": v(28.57, -29.15) * mm, "end": v(28.57, -27.67) * mm});
            skLineSegment(sketch, "E384", {"start": v(28.57, -27.67) * mm, "end": v(34.5, -24.77) * mm});
            skLineSegment(sketch, "E385", {"start": v(32.54, -27.64) * mm, "end": v(30.8, -28.26) * mm});
            skLineSegment(sketch, "E386", {"start": v(30.8, -28.26) * mm, "end": v(30.8, -29.86) * mm});
            skLineSegment(sketch, "E387", {"start": v(30.8, -29.86) * mm, "end": v(32.72, -29.25) * mm});
            skLineSegment(sketch, "E388", {"start": v(32.72, -29.25) * mm, "end": v(32.72, -30.9) * mm});
            skLineSegment(sketch, "E389", {"start": v(32.72, -30.9) * mm, "end": v(30.8, -31.62) * mm});
            skLineSegment(sketch, "E390", {"start": v(30.8, -31.62) * mm, "end": v(30.8, -33.14) * mm});
            skLineSegment(sketch, "E391", {"start": v(30.8, -33.14) * mm, "end": v(32.64, -32.27) * mm});
            skLineSegment(sketch, "E392", {"start": v(34.5, -30.28) * mm, "end": v(34.5, -32.94) * mm});
            skLineSegment(sketch, "E393", {"start": v(34.5, -24.77) * mm, "end": v(34.5, -27.93) * mm});
            skLineSegment(sketch, "E394", {"start": v(34.5, -27.93) * mm, "end": v(32.54, -28.83) * mm});
            skLineSegment(sketch, "E395", {"start": v(32.54, -28.83) * mm, "end": v(32.54, -27.64) * mm});
            skLineSegment(sketch, "E396", {"start": v(32.64, -32.27) * mm, "end": v(32.64, -31.12) * mm});
            skLineSegment(sketch, "E397", {"start": v(32.64, -31.12) * mm, "end": v(34.5, -30.28) * mm});
            skLineSegment(sketch, "E398", {"start": v(35.7, -29.54) * mm, "end": v(37.63, -28.47) * mm});
            skLineSegment(sketch, "E399", {"start": v(37.63, -28.47) * mm, "end": v(37.63, -29.5) * mm});
            skLineSegment(sketch, "E400", {"start": v(37.63, -29.5) * mm, "end": v(39.18, -28.5) * mm});
            skLineSegment(sketch, "E401", {"start": v(39.18, -28.5) * mm, "end": v(39.18, -27.17) * mm});
            skLineSegment(sketch, "E402", {"start": v(39.18, -27.17) * mm, "end": v(36.65, -28.58) * mm});
            skLineSegment(sketch, "E403", {"start": v(36.65, -28.58) * mm, "end": v(35.85, -28.23) * mm});
            skLineSegment(sketch, "E404", {"start": v(35.85, -28.23) * mm, "end": v(35.85, -24.64) * mm});
            skLineSegment(sketch, "E405", {"start": v(35.85, -24.64) * mm, "end": v(36.54, -23.5) * mm});
            skLineSegment(sketch, "E406", {"start": v(36.54, -23.5) * mm, "end": v(40.72, -20.77) * mm});
            skLineSegment(sketch, "E407", {"start": v(40.72, -20.77) * mm, "end": v(40.72, -23.7) * mm});
            skLineSegment(sketch, "E408", {"start": v(40.72, -23.7) * mm, "end": v(39.18, -24.63) * mm});
            skLineSegment(sketch, "E409", {"start": v(39.18, -24.63) * mm, "end": v(39.18, -23.6) * mm});
            skLineSegment(sketch, "E410", {"start": v(39.18, -23.6) * mm, "end": v(37.67, -24.52) * mm});
            skLineSegment(sketch, "E411", {"start": v(37.67, -24.52) * mm, "end": v(37.67, -26.08) * mm});
            skLineSegment(sketch, "E412", {"start": v(37.67, -26.08) * mm, "end": v(39.48, -24.78) * mm});
            skLineSegment(sketch, "E413", {"start": v(39.48, -24.78) * mm, "end": v(40.89, -24.78) * mm});
            skLineSegment(sketch, "E414", {"start": v(40.89, -24.78) * mm, "end": v(40.89, -28.83) * mm});
            skLineSegment(sketch, "E415", {"start": v(40.89, -28.83) * mm, "end": v(40.06, -29.86) * mm});
            skLineSegment(sketch, "E416", {"start": v(40.06, -29.86) * mm, "end": v(35.7, -32.59) * mm});
            skLineSegment(sketch, "E417", {"start": v(35.7, -32.59) * mm, "end": v(35.7, -29.54) * mm});
            skCircle(sketch, "E418", {"center": v(3.57, -12.27) * mm, "radius": 41.57 * mm});
            skLineSegment(sketch, "E419", {"start": v(-7.34, -33.66) * mm, "end": v(-7.34, -35.36) * mm});
            skFitSpline(sketch, "E420", {"points": [v(15.42, -6.32) * mm, v(16.55, -2.84) * mm], "startDerivative": vector(2.92, -1.7) * mm, "endDerivative": vector(-15.87, 4.57) * mm});
            skFitSpline(sketch, "E421", {"points": [v(13.71, 3.88) * mm, v(1.2, -13.5) * mm], "startDerivative": vector(-12.73, 6.89) * mm, "endDerivative": vector(34.08, -57.43) * mm});
            skLineSegment(sketch, "E422", {"start": v(19.14, -4.43) * mm, "end": v(18.8, -4.24) * mm});
            skLineSegment(sketch, "E423", {"start": v(-6.08, 5.03) * mm, "end": v(-6.08, 5.03) * mm});
            skLineSegment(sketch, "E424.bottom", {"start": v(-2.68, 28.88) * mm, "end": v(9.45, 28.88) * mm});
            skLineSegment(sketch, "E424.top", {"start": v(-2.68, 39.89) * mm, "end": v(9.45, 39.89) * mm});
            skLineSegment(sketch, "E424.left", {"start": v(-2.68, 28.88) * mm, "end": v(-2.68, 39.89) * mm});
            skLineSegment(sketch, "E424.right", {"start": v(9.45, 28.88) * mm, "end": v(9.45, 39.89) * mm});
            skCircle(sketch, "E425", {"center": v(3.39, 34.38) * mm, "radius": 3.58 * mm});
            skPoint(sketch, "E425.centerSnap0", {"position": v(-2.68, 34.38) * mm});
            skPoint(sketch, "E425.centerSnap1", {"position": v(3.39, 39.89) * mm});
            skSolve(sketch);
        }
        {
            var Q0;
            Q0=makeQuery(id+"F0.imprint","IMPRINT",FACE,{"disambiguationData":[TD([[makeQuery(id+"F0.imprint","IMPRINT",EDGE,{"derivedFrom":sQuery(id+"F0.wireOp",EDGE,"E139")}),-1.0]])]});
            var Q1;
            Q1=makeQuery(id+"F0.imprint","IMPRINT",FACE,{"disambiguationData":[TD([[makeQuery(id+"F0.imprint","IMPRINT",EDGE,{"derivedFrom":sQuery(id+"F0.wireOp",EDGE,"E145")}),1.0]])]});
            var Q2;
            Q2=makeQuery(id+"F0.imprint","IMPRINT",FACE,{"disambiguationData":[TD([[makeQuery(id+"F0.imprint","IMPRINT",EDGE,{"derivedFrom":sQuery(id+"F0.wireOp",EDGE,"E152")}),1.0]])]});
            var Q3;
            Q3=makeQuery(id+"F0.imprint","IMPRINT",FACE,{"disambiguationData":[TD([[makeQuery(id+"F0.imprint","IMPRINT",EDGE,{"derivedFrom":sQuery(id+"F0.wireOp",EDGE,"E161")}),1.0]])]});
            var Q4;
            Q4=makeQuery(id+"F0.imprint","IMPRINT",FACE,{"disambiguationData":[TD([[makeQuery(id+"F0.imprint","IMPRINT",EDGE,{"derivedFrom":sQuery(id+"F0.wireOp",EDGE,"E177")}),1.0]])]});
            var Q5;
            {var subQ0=sQuery(id+"F0.wireOp",EDGE,"E135");Q5=makeQuery(id+"F0.imprint","IMPRINT",FACE,{"disambiguationData":[TD([[makeQuery(id+"F0.imprint","IMPRINT",EDGE,{"derivedFrom":subQ0}),-1.0]])]});}
            extrude(context, id + "F1", {"entities" : qUnion([Q0, Q1, Q2, Q3, Q4, Q5]), "depth" : 10.16 * mm, "offsetDistance" : 25.4 * mm});
        }
        {
            var Q0;
            Q0=makeQuery(id+"F0.imprint","IMPRINT",FACE,{"disambiguationData":[TD([[makeQuery(id+"F0.imprint","IMPRINT",EDGE,{"derivedFrom":sQuery(id+"F0.wireOp",EDGE,"E0")}),-1.0]])]});
            var Q1;
            Q1=makeQuery(id+"F0.imprint","IMPRINT",FACE,{"disambiguationData":[TD([[makeQuery(id+"F0.imprint","IMPRINT",EDGE,{"derivedFrom":sQuery(id+"F0.wireOp",EDGE,"E268")}),-1.0]])]});
            var Q2;
            Q2=makeQuery(id+"F0.imprint","IMPRINT",FACE,{"disambiguationData":[TD([[makeQuery(id+"F0.imprint","IMPRINT",EDGE,{"derivedFrom":sQuery(id+"F0.wireOp",EDGE,"E285")}),-1.0]])]});
            var Q3;
            Q3=makeQuery(id+"F0.imprint","IMPRINT",FACE,{"disambiguationData":[TD([[makeQuery(id+"F0.imprint","IMPRINT",EDGE,{"derivedFrom":sQuery(id+"F0.wireOp",EDGE,"E306")}),1.0]])]});
            var Q4;
            Q4=makeQuery(id+"F0.imprint","IMPRINT",FACE,{"disambiguationData":[TD([[makeQuery(id+"F0.imprint","IMPRINT",EDGE,{"derivedFrom":sQuery(id+"F0.wireOp",EDGE,"E289")}),-1.0]])]});
            var Q5;
            {var subQ9=sQuery(id+"F0.wireOp",EDGE,"E379");Q5=makeQuery(id+"F0.imprint","IMPRINT",FACE,{"disambiguationData":[TD([[makeQuery(id+"F0.imprint","IMPRINT",EDGE,{"derivedFrom":subQ9}),-1.0]])]});}
            var Q6;
            Q6=makeQuery(id+"F0.imprint","IMPRINT",FACE,{"disambiguationData":[TD([[makeQuery(id+"F0.imprint","IMPRINT",EDGE,{"derivedFrom":sQuery(id+"F0.wireOp",EDGE,"E172")}),1.0]])]});
            extrude(context, id + "F2", {"entities" : qUnion([Q0, Q1, Q2, Q3, Q4, Q5, Q6]), "depth" : 2.54 * mm, "offsetDistance" : 25.4 * mm});
        }
        {
            var Q0;
            Q0=makeQuery(id+"F2.opExtrude","CAP_FACE",FACE,{"disambiguationData":[OSD([sQuery(id+"F0.wireOp",EDGE,"E0"),sQuery(id+"F0.wireOp",EDGE,"E1"),sQuery(id+"F0.wireOp",EDGE,"E2"),sQuery(id+"F0.wireOp",EDGE,"E3"),sQuery(id+"F0.wireOp",EDGE,"E4"),sQuery(id+"F0.wireOp",EDGE,"E5"),sQuery(id+"F0.wireOp",EDGE,"E6"),sQuery(id+"F0.wireOp",EDGE,"E7"),sQuery(id+"F0.wireOp",EDGE,"E8"),sQuery(id+"F0.wireOp",EDGE,"E9"),sQuery(id+"F0.wireOp",EDGE,"E10"),sQuery(id+"F0.wireOp",EDGE,"E11"),sQuery(id+"F0.wireOp",EDGE,"E12"),sQuery(id+"F0.wireOp",EDGE,"E13"),sQuery(id+"F0.wireOp",EDGE,"E14"),sQuery(id+"F0.wireOp",EDGE,"E15"),sQuery(id+"F0.wireOp",EDGE,"E16"),sQuery(id+"F0.wireOp",EDGE,"E17"),sQuery(id+"F0.wireOp",EDGE,"E18"),sQuery(id+"F0.wireOp",EDGE,"E19"),sQuery(id+"F0.wireOp",EDGE,"E20"),sQuery(id+"F0.wireOp",EDGE,"E21"),sQuery(id+"F0.wireOp",EDGE,"E22"),sQuery(id+"F0.wireOp",EDGE,"E23"),sQuery(id+"F0.wireOp",EDGE,"E24"),sQuery(id+"F0.wireOp",EDGE,"E25"),sQuery(id+"F0.wireOp",EDGE,"E26"),sQuery(id+"F0.wireOp",EDGE,"E27"),sQuery(id+"F0.wireOp",EDGE,"E28"),sQuery(id+"F0.wireOp",EDGE,"E29"),sQuery(id+"F0.wireOp",EDGE,"E30"),sQuery(id+"F0.wireOp",EDGE,"E31"),sQuery(id+"F0.wireOp",EDGE,"E32"),sQuery(id+"F0.wireOp",EDGE,"E33"),sQuery(id+"F0.wireOp",EDGE,"E34"),sQuery(id+"F0.wireOp",EDGE,"E35"),sQuery(id+"F0.wireOp",EDGE,"E36"),sQuery(id+"F0.wireOp",EDGE,"E37"),sQuery(id+"F0.wireOp",EDGE,"E38"),sQuery(id+"F0.wireOp",EDGE,"E39"),sQuery(id+"F0.wireOp",EDGE,"E40"),sQuery(id+"F0.wireOp",EDGE,"E41"),sQuery(id+"F0.wireOp",EDGE,"E42"),sQuery(id+"F0.wireOp",EDGE,"E43"),sQuery(id+"F0.wireOp",EDGE,"E44"),sQuery(id+"F0.wireOp",EDGE,"E45"),sQuery(id+"F0.wireOp",EDGE,"E46"),sQuery(id+"F0.wireOp",EDGE,"E47"),sQuery(id+"F0.wireOp",EDGE,"E48"),sQuery(id+"F0.wireOp",EDGE,"E49"),sQuery(id+"F0.wireOp",EDGE,"E50"),sQuery(id+"F0.wireOp",EDGE,"E51"),sQuery(id+"F0.wireOp",EDGE,"E52"),sQuery(id+"F0.wireOp",EDGE,"E53"),sQuery(id+"F0.wireOp",EDGE,"E54"),sQuery(id+"F0.wireOp",EDGE,"E55"),sQuery(id+"F0.wireOp",EDGE,"E56"),sQuery(id+"F0.wireOp",EDGE,"E57"),sQuery(id+"F0.wireOp",EDGE,"E58"),sQuery(id+"F0.wireOp",EDGE,"E59"),sQuery(id+"F0.wireOp",EDGE,"E60"),sQuery(id+"F0.wireOp",EDGE,"E61"),sQuery(id+"F0.wireOp",EDGE,"E62"),sQuery(id+"F0.wireOp",EDGE,"E63"),sQuery(id+"F0.wireOp",EDGE,"E64"),sQuery(id+"F0.wireOp",EDGE,"E65"),sQuery(id+"F0.wireOp",EDGE,"E66"),sQuery(id+"F0.wireOp",EDGE,"E67"),sQuery(id+"F0.wireOp",EDGE,"E68"),sQuery(id+"F0.wireOp",EDGE,"E69"),sQuery(id+"F0.wireOp",EDGE,"E70"),sQuery(id+"F0.wireOp",EDGE,"E71"),sQuery(id+"F0.wireOp",EDGE,"E72"),sQuery(id+"F0.wireOp",EDGE,"E73"),sQuery(id+"F0.wireOp",EDGE,"E74"),sQuery(id+"F0.wireOp",EDGE,"E75"),sQuery(id+"F0.wireOp",EDGE,"E76"),sQuery(id+"F0.wireOp",EDGE,"E77"),sQuery(id+"F0.wireOp",EDGE,"E78"),sQuery(id+"F0.wireOp",EDGE,"E79"),sQuery(id+"F0.wireOp",EDGE,"E80"),sQuery(id+"F0.wireOp",EDGE,"E81"),sQuery(id+"F0.wireOp",EDGE,"E82"),sQuery(id+"F0.wireOp",EDGE,"E83"),sQuery(id+"F0.wireOp",EDGE,"E84"),sQuery(id+"F0.wireOp",EDGE,"E85"),sQuery(id+"F0.wireOp",EDGE,"E86"),sQuery(id+"F0.wireOp",EDGE,"E87"),sQuery(id+"F0.wireOp",EDGE,"E88"),sQuery(id+"F0.wireOp",EDGE,"E89"),sQuery(id+"F0.wireOp",EDGE,"E90"),sQuery(id+"F0.wireOp",EDGE,"E91"),sQuery(id+"F0.wireOp",EDGE,"E95"),sQuery(id+"F0.wireOp",EDGE,"E96"),sQuery(id+"F0.wireOp",EDGE,"E97"),sQuery(id+"F0.wireOp",EDGE,"E98"),sQuery(id+"F0.wireOp",EDGE,"E99"),sQuery(id+"F0.wireOp",EDGE,"E100"),sQuery(id+"F0.wireOp",EDGE,"E101"),sQuery(id+"F0.wireOp",EDGE,"E102"),sQuery(id+"F0.wireOp",EDGE,"E103"),sQuery(id+"F0.wireOp",EDGE,"E104"),sQuery(id+"F0.wireOp",EDGE,"E105"),sQuery(id+"F0.wireOp",EDGE,"E106"),sQuery(id+"F0.wireOp",EDGE,"E107"),sQuery(id+"F0.wireOp",EDGE,"E108"),sQuery(id+"F0.wireOp",EDGE,"E109"),sQuery(id+"F0.wireOp",EDGE,"E110"),sQuery(id+"F0.wireOp",EDGE,"E111"),sQuery(id+"F0.wireOp",EDGE,"E112"),sQuery(id+"F0.wireOp",EDGE,"E113"),sQuery(id+"F0.wireOp",EDGE,"E114"),sQuery(id+"F0.wireOp",EDGE,"E115"),sQuery(id+"F0.wireOp",EDGE,"E116"),sQuery(id+"F0.wireOp",EDGE,"E117"),sQuery(id+"F0.wireOp",EDGE,"E118"),sQuery(id+"F0.wireOp",EDGE,"E119"),sQuery(id+"F0.wireOp",EDGE,"E120"),sQuery(id+"F0.wireOp",EDGE,"E121"),sQuery(id+"F0.wireOp",EDGE,"E122"),sQuery(id+"F0.wireOp",EDGE,"E123"),sQuery(id+"F0.wireOp",EDGE,"E124"),sQuery(id+"F0.wireOp",EDGE,"E125"),sQuery(id+"F0.wireOp",EDGE,"E126"),sQuery(id+"F0.wireOp",EDGE,"E127"),sQuery(id+"F0.wireOp",EDGE,"E128"),sQuery(id+"F0.wireOp",EDGE,"E129"),sQuery(id+"F0.wireOp",EDGE,"E130"),sQuery(id+"F0.wireOp",EDGE,"E131"),sQuery(id+"F0.wireOp",EDGE,"E132"),sQuery(id+"F0.wireOp",EDGE,"E133"),sQuery(id+"F0.wireOp",EDGE,"E134"),sQuery(id+"F0.wireOp",EDGE,"E164"),sQuery(id+"F0.wireOp",EDGE,"E165"),sQuery(id+"F0.wireOp",EDGE,"E166"),sQuery(id+"F0.wireOp",EDGE,"E167"),sQuery(id+"F0.wireOp",EDGE,"E168"),sQuery(id+"F0.wireOp",EDGE,"E169"),sQuery(id+"F0.wireOp",EDGE,"E170"),sQuery(id+"F0.wireOp",EDGE,"E171"),sQuery(id+"F0.wireOp",EDGE,"E177"),sQuery(id+"F0.wireOp",EDGE,"E178"),sQuery(id+"F0.wireOp",EDGE,"E179"),sQuery(id+"F0.wireOp",EDGE,"E180"),sQuery(id+"F0.wireOp",EDGE,"E181"),sQuery(id+"F0.wireOp",EDGE,"E182"),sQuery(id+"F0.wireOp",EDGE,"E183"),sQuery(id+"F0.wireOp",EDGE,"E184"),sQuery(id+"F0.wireOp",EDGE,"E185"),sQuery(id+"F0.wireOp",EDGE,"E186"),sQuery(id+"F0.wireOp",EDGE,"E187"),sQuery(id+"F0.wireOp",EDGE,"E188"),sQuery(id+"F0.wireOp",EDGE,"E189"),sQuery(id+"F0.wireOp",EDGE,"E190"),sQuery(id+"F0.wireOp",EDGE,"E191"),sQuery(id+"F0.wireOp",EDGE,"E192"),sQuery(id+"F0.wireOp",EDGE,"E193"),sQuery(id+"F0.wireOp",EDGE,"E194"),sQuery(id+"F0.wireOp",EDGE,"E195"),sQuery(id+"F0.wireOp",EDGE,"E196"),sQuery(id+"F0.wireOp",EDGE,"E197"),sQuery(id+"F0.wireOp",EDGE,"E198"),sQuery(id+"F0.wireOp",EDGE,"E199"),sQuery(id+"F0.wireOp",EDGE,"E200"),sQuery(id+"F0.wireOp",EDGE,"E201"),sQuery(id+"F0.wireOp",EDGE,"E202"),sQuery(id+"F0.wireOp",EDGE,"E203"),sQuery(id+"F0.wireOp",EDGE,"E204"),sQuery(id+"F0.wireOp",EDGE,"E205"),sQuery(id+"F0.wireOp",EDGE,"E206"),sQuery(id+"F0.wireOp",EDGE,"E207"),sQuery(id+"F0.wireOp",EDGE,"E208"),sQuery(id+"F0.wireOp",EDGE,"E209"),sQuery(id+"F0.wireOp",EDGE,"E210"),sQuery(id+"F0.wireOp",EDGE,"E211"),sQuery(id+"F0.wireOp",EDGE,"E212"),sQuery(id+"F0.wireOp",EDGE,"E213"),sQuery(id+"F0.wireOp",EDGE,"E214"),sQuery(id+"F0.wireOp",EDGE,"E215"),sQuery(id+"F0.wireOp",EDGE,"E216"),sQuery(id+"F0.wireOp",EDGE,"E217"),sQuery(id+"F0.wireOp",EDGE,"E218"),sQuery(id+"F0.wireOp",EDGE,"E219"),sQuery(id+"F0.wireOp",EDGE,"E220"),sQuery(id+"F0.wireOp",EDGE,"E221"),sQuery(id+"F0.wireOp",EDGE,"E222"),sQuery(id+"F0.wireOp",EDGE,"E223"),sQuery(id+"F0.wireOp",EDGE,"E224"),sQuery(id+"F0.wireOp",EDGE,"E225"),sQuery(id+"F0.wireOp",EDGE,"E226"),sQuery(id+"F0.wireOp",EDGE,"E227"),sQuery(id+"F0.wireOp",EDGE,"E228"),sQuery(id+"F0.wireOp",EDGE,"E229"),sQuery(id+"F0.wireOp",EDGE,"E230"),sQuery(id+"F0.wireOp",EDGE,"E231"),sQuery(id+"F0.wireOp",EDGE,"E232"),sQuery(id+"F0.wireOp",EDGE,"E233"),sQuery(id+"F0.wireOp",EDGE,"E234"),sQuery(id+"F0.wireOp",EDGE,"E235"),sQuery(id+"F0.wireOp",EDGE,"E236"),sQuery(id+"F0.wireOp",EDGE,"E237"),sQuery(id+"F0.wireOp",EDGE,"E238"),sQuery(id+"F0.wireOp",EDGE,"E239"),sQuery(id+"F0.wireOp",EDGE,"E240"),sQuery(id+"F0.wireOp",EDGE,"E241"),sQuery(id+"F0.wireOp",EDGE,"E242"),sQuery(id+"F0.wireOp",EDGE,"E243"),sQuery(id+"F0.wireOp",EDGE,"E244"),sQuery(id+"F0.wireOp",EDGE,"E245"),sQuery(id+"F0.wireOp",EDGE,"E246"),sQuery(id+"F0.wireOp",EDGE,"E247"),sQuery(id+"F0.wireOp",EDGE,"E248"),sQuery(id+"F0.wireOp",EDGE,"E249"),sQuery(id+"F0.wireOp",EDGE,"E250"),sQuery(id+"F0.wireOp",EDGE,"E251"),sQuery(id+"F0.wireOp",EDGE,"E252"),sQuery(id+"F0.wireOp",EDGE,"E253"),sQuery(id+"F0.wireOp",EDGE,"E254"),sQuery(id+"F0.wireOp",EDGE,"E255"),sQuery(id+"F0.wireOp",EDGE,"E256"),sQuery(id+"F0.wireOp",EDGE,"E257"),sQuery(id+"F0.wireOp",EDGE,"E258"),sQuery(id+"F0.wireOp",EDGE,"E259"),sQuery(id+"F0.wireOp",EDGE,"E260"),sQuery(id+"F0.wireOp",EDGE,"E261"),sQuery(id+"F0.wireOp",EDGE,"E262"),sQuery(id+"F0.wireOp",EDGE,"E263"),sQuery(id+"F0.wireOp",EDGE,"E264"),sQuery(id+"F0.wireOp",EDGE,"E265"),sQuery(id+"F0.wireOp",EDGE,"E266"),sQuery(id+"F0.wireOp",EDGE,"E267"),sQuery(id+"F0.wireOp",EDGE,"E309"),sQuery(id+"F0.wireOp",EDGE,"E310"),sQuery(id+"F0.wireOp",EDGE,"E311"),sQuery(id+"F0.wireOp",EDGE,"E312"),sQuery(id+"F0.wireOp",EDGE,"E313"),sQuery(id+"F0.wireOp",EDGE,"E314"),sQuery(id+"F0.wireOp",EDGE,"E315"),sQuery(id+"F0.wireOp",EDGE,"E316"),sQuery(id+"F0.wireOp",EDGE,"E317"),sQuery(id+"F0.wireOp",EDGE,"E318"),sQuery(id+"F0.wireOp",EDGE,"E319"),sQuery(id+"F0.wireOp",EDGE,"E320"),sQuery(id+"F0.wireOp",EDGE,"E321"),sQuery(id+"F0.wireOp",EDGE,"E322"),sQuery(id+"F0.wireOp",EDGE,"E323"),sQuery(id+"F0.wireOp",EDGE,"E324"),sQuery(id+"F0.wireOp",EDGE,"E325"),sQuery(id+"F0.wireOp",EDGE,"E326"),sQuery(id+"F0.wireOp",EDGE,"E327"),sQuery(id+"F0.wireOp",EDGE,"E328"),sQuery(id+"F0.wireOp",EDGE,"E329"),sQuery(id+"F0.wireOp",EDGE,"E330"),sQuery(id+"F0.wireOp",EDGE,"E331"),sQuery(id+"F0.wireOp",EDGE,"E332"),sQuery(id+"F0.wireOp",EDGE,"E333"),sQuery(id+"F0.wireOp",EDGE,"E334"),sQuery(id+"F0.wireOp",EDGE,"E335"),sQuery(id+"F0.wireOp",EDGE,"E336"),sQuery(id+"F0.wireOp",EDGE,"E337"),sQuery(id+"F0.wireOp",EDGE,"E338"),sQuery(id+"F0.wireOp",EDGE,"E339"),sQuery(id+"F0.wireOp",EDGE,"E340"),sQuery(id+"F0.wireOp",EDGE,"E341"),sQuery(id+"F0.wireOp",EDGE,"E342"),sQuery(id+"F0.wireOp",EDGE,"E343"),sQuery(id+"F0.wireOp",EDGE,"E344"),sQuery(id+"F0.wireOp",EDGE,"E345"),sQuery(id+"F0.wireOp",EDGE,"E346"),sQuery(id+"F0.wireOp",EDGE,"E347"),sQuery(id+"F0.wireOp",EDGE,"E348"),sQuery(id+"F0.wireOp",EDGE,"E349"),sQuery(id+"F0.wireOp",EDGE,"E350"),sQuery(id+"F0.wireOp",EDGE,"E351"),sQuery(id+"F0.wireOp",EDGE,"E352"),sQuery(id+"F0.wireOp",EDGE,"E353"),sQuery(id+"F0.wireOp",EDGE,"E354"),sQuery(id+"F0.wireOp",EDGE,"E358"),sQuery(id+"F0.wireOp",EDGE,"E359"),sQuery(id+"F0.wireOp",EDGE,"E360"),sQuery(id+"F0.wireOp",EDGE,"E361"),sQuery(id+"F0.wireOp",EDGE,"E362"),sQuery(id+"F0.wireOp",EDGE,"E363"),sQuery(id+"F0.wireOp",EDGE,"E364"),sQuery(id+"F0.wireOp",EDGE,"E366"),sQuery(id+"F0.wireOp",EDGE,"E367"),sQuery(id+"F0.wireOp",EDGE,"E368"),sQuery(id+"F0.wireOp",EDGE,"E369"),sQuery(id+"F0.wireOp",EDGE,"E370"),sQuery(id+"F0.wireOp",EDGE,"E371"),sQuery(id+"F0.wireOp",EDGE,"E372"),sQuery(id+"F0.wireOp",EDGE,"E373"),sQuery(id+"F0.wireOp",EDGE,"E374"),sQuery(id+"F0.wireOp",EDGE,"E375"),sQuery(id+"F0.wireOp",EDGE,"E376"),sQuery(id+"F0.wireOp",EDGE,"E377"),sQuery(id+"F0.wireOp",EDGE,"E378"),sQuery(id+"F0.wireOp",EDGE,"E383"),sQuery(id+"F0.wireOp",EDGE,"E384"),sQuery(id+"F0.wireOp",EDGE,"E387"),sQuery(id+"F0.wireOp",EDGE,"E388"),sQuery(id+"F0.wireOp",EDGE,"E389"),sQuery(id+"F0.wireOp",EDGE,"E391"),sQuery(id+"F0.wireOp",EDGE,"E392"),sQuery(id+"F0.wireOp",EDGE,"E393"),sQuery(id+"F0.wireOp",EDGE,"E394"),sQuery(id+"F0.wireOp",EDGE,"E395"),sQuery(id+"F0.wireOp",EDGE,"E396"),sQuery(id+"F0.wireOp",EDGE,"E397"),sQuery(id+"F0.wireOp",EDGE,"E398"),sQuery(id+"F0.wireOp",EDGE,"E399"),sQuery(id+"F0.wireOp",EDGE,"E400"),sQuery(id+"F0.wireOp",EDGE,"E401"),sQuery(id+"F0.wireOp",EDGE,"E402"),sQuery(id+"F0.wireOp",EDGE,"E403"),sQuery(id+"F0.wireOp",EDGE,"E404"),sQuery(id+"F0.wireOp",EDGE,"E405"),sQuery(id+"F0.wireOp",EDGE,"E406"),sQuery(id+"F0.wireOp",EDGE,"E407"),sQuery(id+"F0.wireOp",EDGE,"E408"),sQuery(id+"F0.wireOp",EDGE,"E409"),sQuery(id+"F0.wireOp",EDGE,"E410"),sQuery(id+"F0.wireOp",EDGE,"E411"),sQuery(id+"F0.wireOp",EDGE,"E412"),sQuery(id+"F0.wireOp",EDGE,"E413"),sQuery(id+"F0.wireOp",EDGE,"E414"),sQuery(id+"F0.wireOp",EDGE,"E415"),sQuery(id+"F0.wireOp",EDGE,"E416"),sQuery(id+"F0.wireOp",EDGE,"E417"),sQuery(id+"F0.wireOp",EDGE,"E418"),sQuery(id+"F0.wireOp",EDGE,"E420"),sQuery(id+"F0.wireOp",EDGE,"E421"),sQuery(id+"F0.wireOp",EDGE,"E422"),sQuery(id+"F0.wireOp",EDGE,"E424.bottom")])],"isStart":false});
            var sketch = newSketch(context, id + "F3", { "sketchPlane" : qUnion([Q0])});
            skFitSpline(sketch, "E426.0", {"points": [v(-21.2, 7.76) * mm, v(-19.86, 9.4) * mm, v(-17.62, 9.5) * mm, v(-16.87, 8.87) * mm]});
            skFitSpline(sketch, "E427.0", {"points": [v(-20.5, 4.52) * mm, v(-23.51, 5.48) * mm, v(-22.54, 7.4) * mm, v(-21.2, 7.76) * mm]});
            skFitSpline(sketch, "E428.0", {"points": [v(-20.5, 4.52) * mm, v(-18.63, 2.92) * mm, v(-17.24, 3.18) * mm, v(-16, 4.62) * mm]});
            skFitSpline(sketch, "E429.0", {"points": [v(-15.62, 6.25) * mm, v(-16.26, 6.2) * mm, v(-15.88, 5.16) * mm, v(-16, 4.62) * mm]});
            skFitSpline(sketch, "E430.0", {"points": [v(-16.87, 8.87) * mm, v(-14.07, 8.07) * mm, v(-15.9, 6.85) * mm, v(-15.62, 6.25) * mm]});
            skSolve(sketch);
        }
        {
            var Q0;
            Q0=makeQuery(id+"F3.imprint","IMPRINT",FACE,{"disambiguationData":[TD([[makeQuery(id+"F3.imprint","IMPRINT",EDGE,{"derivedFrom":sQuery(id+"F3.wireOp",EDGE,"E426.0")}),-1.0]])]});
            extrude(context, id + "F4", {"entities" : qUnion([Q0]), "operationType" : NewBodyOperationType.ADD, "depth" : 7.64 * mm, "offsetDistance" : 25 * mm});
        }
        {
            var Q0;
            {var subQ0=sQuery(id+"F0.wireOp",EDGE,"E191");Q0=makeQuery(id+"F0.imprint","IMPRINT",FACE,{"disambiguationData":[TD([[makeQuery(id+"F0.imprint","IMPRINT",EDGE,{"derivedFrom":subQ0}),-1.0]])]});}
            var Q1;
            {var subQ0=sQuery(id+"F0.wireOp",EDGE,"E186");var subQ9=sQuery(id+"F0.wireOp",EDGE,"E129");var subQ10=makeQuery(id+"F0.imprint","INTERSECT",VERTEX,{"derivedFrom":[subQ9,subQ0]});Q1=makeQuery(id+"F0.imprint","IMPRINT",FACE,{"disambiguationData":[TD([[makeQuery(id+"F0.imprint","IMPRINT",EDGE,{"disambiguationData":[TD([[subQ10,-1.0]])],"derivedFrom":subQ9}),-1.0]])]});}
            var Q2;
            {var subQ1=sQuery(id+"F0.wireOp",EDGE,"E187");Q2=makeQuery(id+"F0.imprint","IMPRINT",FACE,{"disambiguationData":[TD([[makeQuery(id+"F0.imprint","IMPRINT",EDGE,{"derivedFrom":subQ1}),-1.0]])]});}
            extrude(context, id + "F5", {"entities" : qUnion([Q0, Q1, Q2]), "operationType" : NewBodyOperationType.ADD, "depth" : 10.16 * mm, "offsetDistance" : 25.4 * mm});
        }
        {
            var Q0;
            Q0=makeQuery(id+"F0.imprint","IMPRINT",FACE,{"disambiguationData":[TD([[makeQuery(id+"F0.imprint","IMPRINT",EDGE,{"derivedFrom":sQuery(id+"F0.wireOp",EDGE,"E128")}),-1.0]])]});
            extrude(context, id + "F6", {"entities" : qUnion([Q0]), "operationType" : NewBodyOperationType.ADD, "depth" : 7.62 * mm, "offsetDistance" : 25.4 * mm});
        }
        {
            var Q0;
            Q0=makeQuery(id+"F0.imprint","IMPRINT",FACE,{"disambiguationData":[TD([[makeQuery(id+"F0.imprint","IMPRINT",EDGE,{"derivedFrom":sQuery(id+"F0.wireOp",EDGE,"E0")}),1.0]])]});
            var Q1;
            Q1=makeQuery(id+"F0.imprint","IMPRINT",FACE,{"disambiguationData":[TD([[makeQuery(id+"F0.imprint","IMPRINT",EDGE,{"derivedFrom":sQuery(id+"F0.wireOp",EDGE,"E28")}),1.0]])]});
            var Q2;
            Q2=makeQuery(id+"F0.imprint","IMPRINT",FACE,{"disambiguationData":[TD([[makeQuery(id+"F0.imprint","IMPRINT",EDGE,{"derivedFrom":sQuery(id+"F0.wireOp",EDGE,"E40")}),1.0]])]});
            var Q3;
            Q3=makeQuery(id+"F0.imprint","IMPRINT",FACE,{"disambiguationData":[TD([[makeQuery(id+"F0.imprint","IMPRINT",EDGE,{"derivedFrom":sQuery(id+"F0.wireOp",EDGE,"E55")}),1.0]])]});
            var Q4;
            Q4=makeQuery(id+"F0.imprint","IMPRINT",FACE,{"disambiguationData":[TD([[makeQuery(id+"F0.imprint","IMPRINT",EDGE,{"derivedFrom":sQuery(id+"F0.wireOp",EDGE,"E83")}),-1.0]])]});
            var Q5;
            Q5=makeQuery(id+"F0.imprint","IMPRINT",FACE,{"disambiguationData":[TD([[makeQuery(id+"F0.imprint","IMPRINT",EDGE,{"derivedFrom":sQuery(id+"F0.wireOp",EDGE,"E100")}),-1.0]])]});
            var Q6;
            Q6=makeQuery(id+"F0.imprint","IMPRINT",FACE,{"disambiguationData":[TD([[makeQuery(id+"F0.imprint","IMPRINT",EDGE,{"derivedFrom":sQuery(id+"F0.wireOp",EDGE,"E222")}),1.0]])]});
            var Q7;
            Q7=makeQuery(id+"F0.imprint","IMPRINT",FACE,{"disambiguationData":[TD([[makeQuery(id+"F0.imprint","IMPRINT",EDGE,{"derivedFrom":sQuery(id+"F0.wireOp",EDGE,"E250")}),1.0]])]});
            var Q8;
            Q8=makeQuery(id+"F0.imprint","IMPRINT",FACE,{"disambiguationData":[TD([[makeQuery(id+"F0.imprint","IMPRINT",EDGE,{"derivedFrom":sQuery(id+"F0.wireOp",EDGE,"E268")}),-1.0]])]});
            var Q9;
            Q9=makeQuery(id+"F0.imprint","IMPRINT",FACE,{"disambiguationData":[TD([[makeQuery(id+"F0.imprint","IMPRINT",EDGE,{"derivedFrom":sQuery(id+"F0.wireOp",EDGE,"E309")}),1.0]])]});
            var Q10;
            Q10=makeQuery(id+"F0.imprint","IMPRINT",FACE,{"disambiguationData":[TD([[makeQuery(id+"F0.imprint","IMPRINT",EDGE,{"derivedFrom":sQuery(id+"F0.wireOp",EDGE,"E321")}),-1.0]])]});
            var Q11;
            Q11=makeQuery(id+"F0.imprint","IMPRINT",FACE,{"disambiguationData":[TD([[makeQuery(id+"F0.imprint","IMPRINT",EDGE,{"derivedFrom":sQuery(id+"F0.wireOp",EDGE,"E336")}),1.0]])]});
            var Q12;
            Q12=makeQuery(id+"F0.imprint","IMPRINT",FACE,{"disambiguationData":[TD([[makeQuery(id+"F0.imprint","IMPRINT",EDGE,{"derivedFrom":sQuery(id+"F0.wireOp",EDGE,"E358")}),1.0]])]});
            var Q13;
            {var subQ1=sQuery(id+"F0.wireOp",EDGE,"E379");Q13=makeQuery(id+"F0.imprint","IMPRINT",FACE,{"disambiguationData":[TD([[makeQuery(id+"F0.imprint","IMPRINT",EDGE,{"derivedFrom":subQ1}),-1.0]])]});}
            var Q14;
            {var subQ4=sQuery(id+"F0.wireOp",EDGE,"E392");Q14=makeQuery(id+"F0.imprint","IMPRINT",FACE,{"disambiguationData":[TD([[makeQuery(id+"F0.imprint","IMPRINT",EDGE,{"derivedFrom":subQ4}),-1.0]])]});}
            var Q15;
            {var subQ1=sQuery(id+"F0.wireOp",EDGE,"E393");Q15=makeQuery(id+"F0.imprint","IMPRINT",FACE,{"disambiguationData":[TD([[makeQuery(id+"F0.imprint","IMPRINT",EDGE,{"derivedFrom":subQ1}),-1.0]])]});}
            var Q16;
            Q16=makeQuery(id+"F0.imprint","IMPRINT",FACE,{"disambiguationData":[TD([[makeQuery(id+"F0.imprint","IMPRINT",EDGE,{"derivedFrom":sQuery(id+"F0.wireOp",EDGE,"E398")}),-1.0]])]});
            var Q17;
            {var subQ5=sQuery(id+"F0.wireOp",EDGE,"E388");Q17=makeQuery(id+"F0.imprint","IMPRINT",FACE,{"disambiguationData":[TD([[makeQuery(id+"F0.imprint","IMPRINT",EDGE,{"derivedFrom":subQ5}),-1.0]])]});}
            var Q18;
            Q18=makeQuery(id+"F0.imprint","IMPRINT",FACE,{"disambiguationData":[TD([[makeQuery(id+"F0.imprint","IMPRINT",EDGE,{"derivedFrom":sQuery(id+"F0.wireOp",EDGE,"E289")}),-1.0]])]});
            var Q19;
            {var subQ5=sQuery(id+"F0.wireOp",EDGE,"E365");Q19=makeQuery(id+"F0.imprint","IMPRINT",FACE,{"disambiguationData":[TD([[makeQuery(id+"F0.imprint","IMPRINT",EDGE,{"derivedFrom":subQ5}),1.0]])]});}
            var Q20;
            {var subQ0=sQuery(id+"F0.wireOp",EDGE,"E384");var subQ1=sQuery(id+"F0.wireOp",EDGE,"E130");var subQ2=makeQuery(id+"F0.imprint","INTERSECT",VERTEX,{"derivedFrom":[subQ1,subQ0]});Q20=makeQuery(id+"F0.imprint","IMPRINT",FACE,{"disambiguationData":[TD([[makeQuery(id+"F0.imprint","IMPRINT",EDGE,{"disambiguationData":[TD([[subQ2,-1.0]])],"derivedFrom":subQ1}),-1.0]])]});}
            extrude(context, id + "F7", {"entities" : qUnion([Q0, Q1, Q2, Q3, Q4, Q5, Q6, Q7, Q8, Q9, Q10, Q11, Q12, Q13, Q14, Q15, Q16, Q17, Q18, Q19, Q20]), "operationType" : NewBodyOperationType.ADD, "depth" : 7.62 * mm, "offsetDistance" : 25.4 * mm});
        }
        {
            var Q0;
            {var subQ13=sQuery(id+"F0.wireOp",EDGE,"E131");Q0=makeQuery(id+"F0.imprint","IMPRINT",FACE,{"disambiguationData":[TD([[makeQuery(id+"F0.imprint","IMPRINT",EDGE,{"derivedFrom":subQ13}),1.0]])]});}
            var Q1;
            {var subQ5=sQuery(id+"F0.wireOp",EDGE,"E390");Q1=makeQuery(id+"F0.imprint","IMPRINT",FACE,{"disambiguationData":[TD([[makeQuery(id+"F0.imprint","IMPRINT",EDGE,{"derivedFrom":subQ5}),1.0]])]});}
            var Q2;
            {var subQ4=sQuery(id+"F0.wireOp",EDGE,"E385");Q2=makeQuery(id+"F0.imprint","IMPRINT",FACE,{"disambiguationData":[TD([[makeQuery(id+"F0.imprint","IMPRINT",EDGE,{"derivedFrom":subQ4}),1.0]])]});}
            var Q3;
            {var subQ1=sQuery(id+"F0.wireOp",EDGE,"E189");var subQ7=sQuery(id+"F0.wireOp",EDGE,"E129");var subQ8=makeQuery(id+"F0.imprint","INTERSECT",VERTEX,{"derivedFrom":[subQ7,subQ1]});Q3=makeQuery(id+"F0.imprint","IMPRINT",FACE,{"disambiguationData":[TD([[makeQuery(id+"F0.imprint","IMPRINT",EDGE,{"disambiguationData":[TD([[subQ8,-1.0]])],"derivedFrom":subQ7}),-1.0]])]});}
            extrude(context, id + "F8", {"entities" : qUnion([Q0, Q1, Q2, Q3]), "operationType" : NewBodyOperationType.ADD, "depth" : 5.08 * mm, "offsetDistance" : 25.4 * mm});
        }
        {
            var Q0;
            Q0=makeQuery(id+"F0.imprint","IMPRINT",FACE,{"disambiguationData":[TD([[makeQuery(id+"F0.imprint","IMPRINT",EDGE,{"derivedFrom":sQuery(id+"F0.wireOp",EDGE,"E424.top")}),-1.0]])]});
            var Q1;
            {var subQ0=sQuery(id+"F0.wireOp",EDGE,"E424.bottom");var subQ1=sQuery(id+"F0.wireOp",EDGE,"E418");var subQ2=makeQuery(id+"F0.imprint","INTERSECT",VERTEX,{"disambiguationData":[OD(0.0)],"derivedFrom":[subQ1,subQ0]});Q1=makeQuery(id+"F0.imprint","IMPRINT",FACE,{"disambiguationData":[TD([[makeQuery(id+"F0.imprint","IMPRINT",EDGE,{"disambiguationData":[TD([[subQ2,1.0]])],"derivedFrom":subQ1}),1.0]])]});}
            extrude(context, id + "F9", {"entities" : qUnion([Q0, Q1]), "operationType" : NewBodyOperationType.ADD, "depth" : 2.54 * mm, "offsetDistance" : 25.4 * mm});
        }
        {
            var Q0;
            {var subQ8=sQuery(id+"F0.wireOp",EDGE,"E196");Q0=makeQuery(id+"F0.imprint","IMPRINT",FACE,{"disambiguationData":[TD([[makeQuery(id+"F0.imprint","IMPRINT",EDGE,{"derivedFrom":subQ8}),-1.0]])]});}
            var Q1;
            Q1=makeQuery(id+"F0.imprint","IMPRINT",FACE,{"disambiguationData":[TD([[makeQuery(id+"F0.imprint","IMPRINT",EDGE,{"derivedFrom":sQuery(id+"F0.wireOp",EDGE,"E161")}),-1.0]])]});
            var Q2;
            {var subQ1=sQuery(id+"F0.wireOp",EDGE,"E210");Q2=makeQuery(id+"F0.imprint","IMPRINT",FACE,{"disambiguationData":[TD([[makeQuery(id+"F0.imprint","IMPRINT",EDGE,{"derivedFrom":subQ1}),-1.0]])]});}
            var Q3;
            {var subQ0=sQuery(id+"F0.wireOp",EDGE,"E180");var subQ1=sQuery(id+"F0.wireOp",EDGE,"E179");var subQ2=makeQuery(id+"F0.imprint","INTERSECT",VERTEX,{"derivedFrom":[subQ1,subQ0]});Q3=makeQuery(id+"F0.imprint","IMPRINT",FACE,{"disambiguationData":[TD([[makeQuery(id+"F0.imprint","IMPRINT",EDGE,{"disambiguationData":[TD([[subQ2,1.0]])],"derivedFrom":subQ1}),1.0]])]});}
            var Q4;
            {var subQ0=sQuery(id+"F0.wireOp",EDGE,"E349");var subQ1=sQuery(id+"F0.wireOp",EDGE,"E204");var subQ2=makeQuery(id+"F0.imprint","INTERSECT",VERTEX,{"derivedFrom":[subQ1,subQ0]});Q4=makeQuery(id+"F0.imprint","IMPRINT",FACE,{"disambiguationData":[TD([[makeQuery(id+"F0.imprint","IMPRINT",EDGE,{"disambiguationData":[TD([[subQ2,-1.0]])],"derivedFrom":subQ1}),-1.0]])]});}
            extrude(context, id + "F10", {"entities" : qUnion([Q0, Q1, Q2, Q3, Q4]), "operationType" : NewBodyOperationType.ADD, "depth" : 5.08 * mm, "offsetDistance" : 25.4 * mm});
        }
    });
